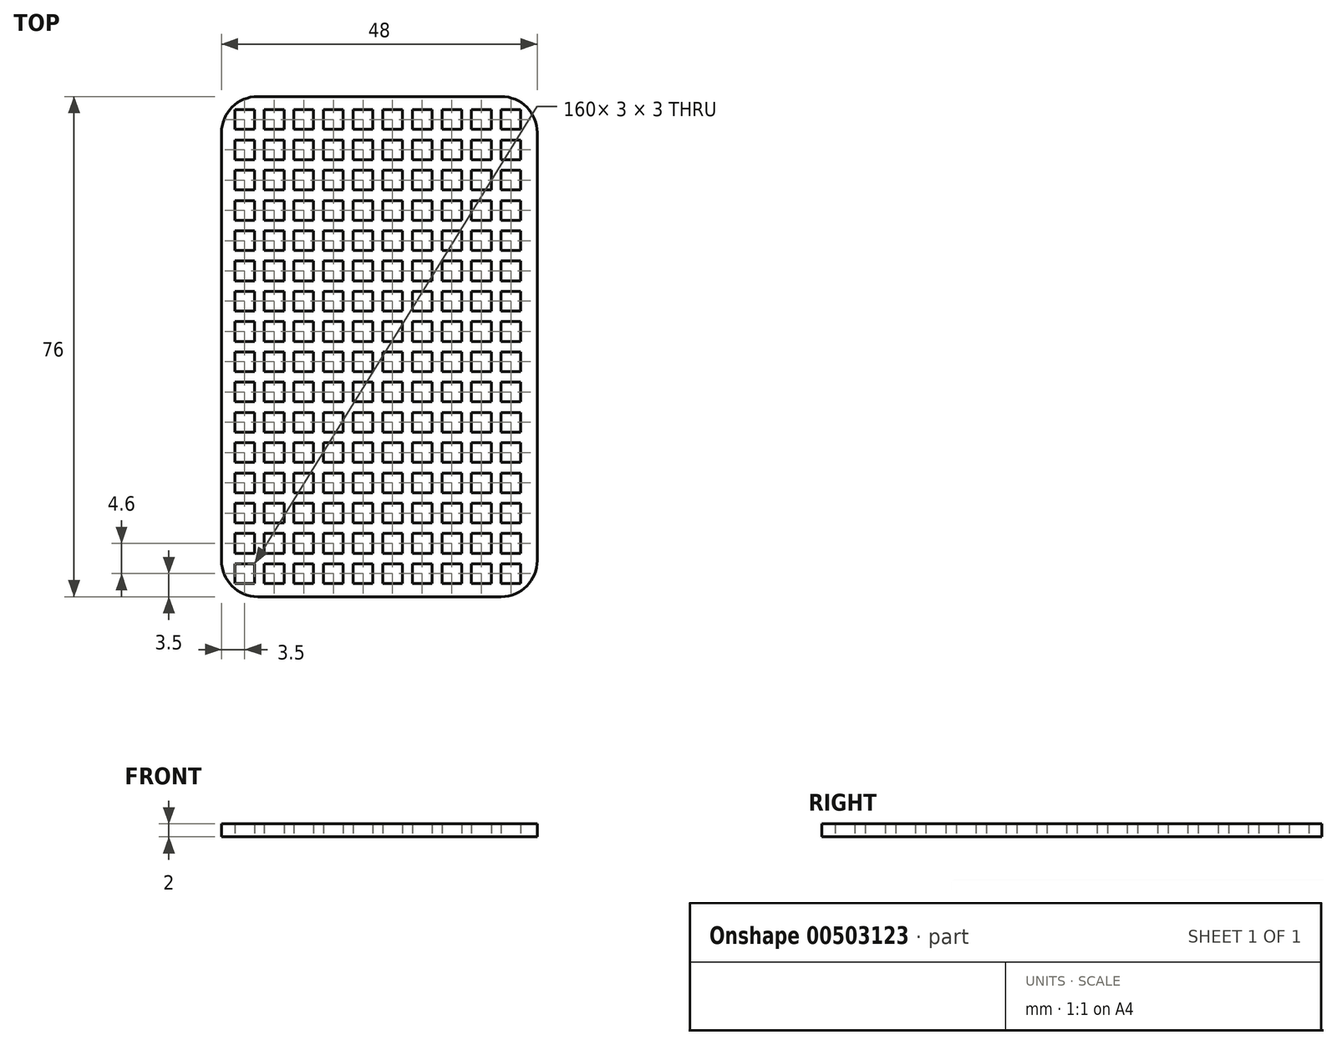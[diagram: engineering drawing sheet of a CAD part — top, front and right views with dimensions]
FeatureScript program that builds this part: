
annotation { "Feature Type Name" : "Feature", "Feature Type Description" : "" }
export const myFeature = defineFeature(function(context is Context, id is Id, definition is map)
    precondition{}
    {
        {
            var Q0;
            Q0=qCreatedBy(makeId("Top.planeOp"),FACE);
            var sketch = newSketch(context, id + "F0", { "sketchPlane" : qUnion([Q0])});
            skLineSegment(sketch, "E0.bottom", {"start": v(18.5, -38) * mm, "end": v(-18.5, -38) * mm});
            skLineSegment(sketch, "E0.top", {"start": v(18.5, 38) * mm, "end": v(-18.5, 38) * mm});
            skLineSegment(sketch, "E0.left", {"start": v(24, -32.5) * mm, "end": v(24, 32.5) * mm});
            skLineSegment(sketch, "E0.right", {"start": v(-24, -32.5) * mm, "end": v(-24, 32.5) * mm});
            skPoint(sketch, "E0.middle", {"position": v(-20.5, 34.5) * mm});
            skPoint(sketch, "E1.visualSharp", {"position": v(-24, 38) * mm});
            skArc(sketch, "E1.filletArc", {"start": v(-18.5, 38) * mm, "mid": v(-22.39, 36.39) * mm, "end": v(-24, 32.5) * mm});
            skPoint(sketch, "E2.visualSharp", {"position": v(24, 38) * mm});
            skArc(sketch, "E2.filletArc", {"start": v(24, 32.5) * mm, "mid": v(22.39, 36.39) * mm, "end": v(18.5, 38) * mm});
            skPoint(sketch, "E3.visualSharp", {"position": v(24, -38) * mm});
            skArc(sketch, "E3.filletArc", {"start": v(18.5, -38) * mm, "mid": v(22.39, -36.39) * mm, "end": v(24, -32.5) * mm});
            skPoint(sketch, "E4.visualSharp", {"position": v(-24, -38) * mm});
            skArc(sketch, "E4.filletArc", {"start": v(-24, -32.5) * mm, "mid": v(-22.39, -36.39) * mm, "end": v(-18.5, -38) * mm});
            skLineSegment(sketch, "E5.bottom", {"start": v(-19, 33) * mm, "end": v(-22, 33) * mm});
            skLineSegment(sketch, "E5.top", {"start": v(-19, 36) * mm, "end": v(-22, 36) * mm});
            skLineSegment(sketch, "E5.left", {"start": v(-19, 33) * mm, "end": v(-19, 36) * mm});
            skLineSegment(sketch, "E5.right", {"start": v(-22, 33) * mm, "end": v(-22, 36) * mm});
            skPoint(sketch, "E6", {"position": v(-22, 36) * mm});
            skPoint(sketch, "E7", {"position": v(52.1, 10.35) * mm});
            skPoint(sketch, "E8.0.1.0", {"position": v(-20.5, 29.9) * mm});
            skLineSegment(sketch, "E8.0.1.1", {"start": v(-22, 28.4) * mm, "end": v(-22, 31.4) * mm});
            skLineSegment(sketch, "E8.0.1.2", {"start": v(-19, 28.4) * mm, "end": v(-19, 31.4) * mm});
            skLineSegment(sketch, "E8.0.1.3", {"start": v(-19, 31.4) * mm, "end": v(-22, 31.4) * mm});
            skLineSegment(sketch, "E8.0.1.4", {"start": v(-19, 28.4) * mm, "end": v(-22, 28.4) * mm});
            skPoint(sketch, "E8.0.1.5", {"position": v(-22, 31.4) * mm});
            skPoint(sketch, "E8.0.1.6", {"position": v(-20.5, 29.9) * mm});
            skPoint(sketch, "E8.0.1.7", {"position": v(-20.5, 29.9) * mm});
            skPoint(sketch, "E8.0.2.0", {"position": v(-20.5, 25.3) * mm});
            skLineSegment(sketch, "E8.0.2.1", {"start": v(-22, 23.8) * mm, "end": v(-22, 26.8) * mm});
            skLineSegment(sketch, "E8.0.2.2", {"start": v(-19, 23.8) * mm, "end": v(-19, 26.8) * mm});
            skLineSegment(sketch, "E8.0.2.3", {"start": v(-19, 26.8) * mm, "end": v(-22, 26.8) * mm});
            skLineSegment(sketch, "E8.0.2.4", {"start": v(-19, 23.8) * mm, "end": v(-22, 23.8) * mm});
            skPoint(sketch, "E8.0.2.5", {"position": v(-22, 26.8) * mm});
            skPoint(sketch, "E8.0.2.6", {"position": v(-20.5, 25.3) * mm});
            skPoint(sketch, "E8.0.2.7", {"position": v(-20.5, 25.3) * mm});
            skPoint(sketch, "E8.0.3.0", {"position": v(-20.5, 20.7) * mm});
            skLineSegment(sketch, "E8.0.3.1", {"start": v(-22, 19.2) * mm, "end": v(-22, 22.2) * mm});
            skLineSegment(sketch, "E8.0.3.2", {"start": v(-19, 19.2) * mm, "end": v(-19, 22.2) * mm});
            skLineSegment(sketch, "E8.0.3.3", {"start": v(-19, 22.2) * mm, "end": v(-22, 22.2) * mm});
            skLineSegment(sketch, "E8.0.3.4", {"start": v(-19, 19.2) * mm, "end": v(-22, 19.2) * mm});
            skPoint(sketch, "E8.0.3.5", {"position": v(-22, 22.2) * mm});
            skPoint(sketch, "E8.0.3.6", {"position": v(-20.5, 20.7) * mm});
            skPoint(sketch, "E8.0.3.7", {"position": v(-20.5, 20.7) * mm});
            skPoint(sketch, "E8.0.4.0", {"position": v(-20.5, 16.1) * mm});
            skLineSegment(sketch, "E8.0.4.1", {"start": v(-22, 14.6) * mm, "end": v(-22, 17.6) * mm});
            skLineSegment(sketch, "E8.0.4.2", {"start": v(-19, 14.6) * mm, "end": v(-19, 17.6) * mm});
            skLineSegment(sketch, "E8.0.4.3", {"start": v(-19, 17.6) * mm, "end": v(-22, 17.6) * mm});
            skLineSegment(sketch, "E8.0.4.4", {"start": v(-19, 14.6) * mm, "end": v(-22, 14.6) * mm});
            skPoint(sketch, "E8.0.4.5", {"position": v(-22, 17.6) * mm});
            skPoint(sketch, "E8.0.4.6", {"position": v(-20.5, 16.1) * mm});
            skPoint(sketch, "E8.0.4.7", {"position": v(-20.5, 16.1) * mm});
            skPoint(sketch, "E8.0.5.0", {"position": v(-20.5, 11.5) * mm});
            skLineSegment(sketch, "E8.0.5.1", {"start": v(-22, 10) * mm, "end": v(-22, 13) * mm});
            skLineSegment(sketch, "E8.0.5.2", {"start": v(-19, 10) * mm, "end": v(-19, 13) * mm});
            skLineSegment(sketch, "E8.0.5.3", {"start": v(-19, 13) * mm, "end": v(-22, 13) * mm});
            skLineSegment(sketch, "E8.0.5.4", {"start": v(-19, 10) * mm, "end": v(-22, 10) * mm});
            skPoint(sketch, "E8.0.5.5", {"position": v(-22, 13) * mm});
            skPoint(sketch, "E8.0.5.6", {"position": v(-20.5, 11.5) * mm});
            skPoint(sketch, "E8.0.5.7", {"position": v(-20.5, 11.5) * mm});
            skPoint(sketch, "E8.0.6.0", {"position": v(-20.5, 6.9) * mm});
            skLineSegment(sketch, "E8.0.6.1", {"start": v(-22, 5.4) * mm, "end": v(-22, 8.4) * mm});
            skLineSegment(sketch, "E8.0.6.2", {"start": v(-19, 5.4) * mm, "end": v(-19, 8.4) * mm});
            skLineSegment(sketch, "E8.0.6.3", {"start": v(-19, 8.4) * mm, "end": v(-22, 8.4) * mm});
            skLineSegment(sketch, "E8.0.6.4", {"start": v(-19, 5.4) * mm, "end": v(-22, 5.4) * mm});
            skPoint(sketch, "E8.0.6.5", {"position": v(-22, 8.4) * mm});
            skPoint(sketch, "E8.0.6.6", {"position": v(-20.5, 6.9) * mm});
            skPoint(sketch, "E8.0.6.7", {"position": v(-20.5, 6.9) * mm});
            skPoint(sketch, "E8.0.7.0", {"position": v(-20.5, 2.3) * mm});
            skLineSegment(sketch, "E8.0.7.1", {"start": v(-22, 0.8) * mm, "end": v(-22, 3.8) * mm});
            skLineSegment(sketch, "E8.0.7.2", {"start": v(-19, 0.8) * mm, "end": v(-19, 3.8) * mm});
            skLineSegment(sketch, "E8.0.7.3", {"start": v(-19, 3.8) * mm, "end": v(-22, 3.8) * mm});
            skLineSegment(sketch, "E8.0.7.4", {"start": v(-19, 0.8) * mm, "end": v(-22, 0.8) * mm});
            skPoint(sketch, "E8.0.7.5", {"position": v(-22, 3.8) * mm});
            skPoint(sketch, "E8.0.7.6", {"position": v(-20.5, 2.3) * mm});
            skPoint(sketch, "E8.0.7.7", {"position": v(-20.5, 2.3) * mm});
            skPoint(sketch, "E8.0.8.0", {"position": v(-20.5, -2.3) * mm});
            skLineSegment(sketch, "E8.0.8.1", {"start": v(-22, -3.8) * mm, "end": v(-22, -0.8) * mm});
            skLineSegment(sketch, "E8.0.8.2", {"start": v(-19, -3.8) * mm, "end": v(-19, -0.8) * mm});
            skLineSegment(sketch, "E8.0.8.3", {"start": v(-19, -0.8) * mm, "end": v(-22, -0.8) * mm});
            skLineSegment(sketch, "E8.0.8.4", {"start": v(-19, -3.8) * mm, "end": v(-22, -3.8) * mm});
            skPoint(sketch, "E8.0.8.5", {"position": v(-22, -0.8) * mm});
            skPoint(sketch, "E8.0.8.6", {"position": v(-20.5, -2.3) * mm});
            skPoint(sketch, "E8.0.8.7", {"position": v(-20.5, -2.3) * mm});
            skPoint(sketch, "E8.0.9.0", {"position": v(-20.5, -6.9) * mm});
            skLineSegment(sketch, "E8.0.9.1", {"start": v(-22, -8.4) * mm, "end": v(-22, -5.4) * mm});
            skLineSegment(sketch, "E8.0.9.2", {"start": v(-19, -8.4) * mm, "end": v(-19, -5.4) * mm});
            skLineSegment(sketch, "E8.0.9.3", {"start": v(-19, -5.4) * mm, "end": v(-22, -5.4) * mm});
            skLineSegment(sketch, "E8.0.9.4", {"start": v(-19, -8.4) * mm, "end": v(-22, -8.4) * mm});
            skPoint(sketch, "E8.0.9.5", {"position": v(-22, -5.4) * mm});
            skPoint(sketch, "E8.0.9.6", {"position": v(-20.5, -6.9) * mm});
            skPoint(sketch, "E8.0.9.7", {"position": v(-20.5, -6.9) * mm});
            skPoint(sketch, "E8.0.10.0", {"position": v(-20.5, -11.5) * mm});
            skLineSegment(sketch, "E8.0.10.1", {"start": v(-22, -13) * mm, "end": v(-22, -10) * mm});
            skLineSegment(sketch, "E8.0.10.2", {"start": v(-19, -13) * mm, "end": v(-19, -10) * mm});
            skLineSegment(sketch, "E8.0.10.3", {"start": v(-19, -10) * mm, "end": v(-22, -10) * mm});
            skLineSegment(sketch, "E8.0.10.4", {"start": v(-19, -13) * mm, "end": v(-22, -13) * mm});
            skPoint(sketch, "E8.0.10.5", {"position": v(-22, -10) * mm});
            skPoint(sketch, "E8.0.10.6", {"position": v(-20.5, -11.5) * mm});
            skPoint(sketch, "E8.0.10.7", {"position": v(-20.5, -11.5) * mm});
            skPoint(sketch, "E8.0.11.0", {"position": v(-20.5, -16.1) * mm});
            skLineSegment(sketch, "E8.0.11.1", {"start": v(-22, -17.6) * mm, "end": v(-22, -14.6) * mm});
            skLineSegment(sketch, "E8.0.11.2", {"start": v(-19, -17.6) * mm, "end": v(-19, -14.6) * mm});
            skLineSegment(sketch, "E8.0.11.3", {"start": v(-19, -14.6) * mm, "end": v(-22, -14.6) * mm});
            skLineSegment(sketch, "E8.0.11.4", {"start": v(-19, -17.6) * mm, "end": v(-22, -17.6) * mm});
            skPoint(sketch, "E8.0.11.5", {"position": v(-22, -14.6) * mm});
            skPoint(sketch, "E8.0.11.6", {"position": v(-20.5, -16.1) * mm});
            skPoint(sketch, "E8.0.11.7", {"position": v(-20.5, -16.1) * mm});
            skPoint(sketch, "E8.0.12.0", {"position": v(-20.5, -20.7) * mm});
            skLineSegment(sketch, "E8.0.12.1", {"start": v(-22, -22.2) * mm, "end": v(-22, -19.2) * mm});
            skLineSegment(sketch, "E8.0.12.2", {"start": v(-19, -22.2) * mm, "end": v(-19, -19.2) * mm});
            skLineSegment(sketch, "E8.0.12.3", {"start": v(-19, -19.2) * mm, "end": v(-22, -19.2) * mm});
            skLineSegment(sketch, "E8.0.12.4", {"start": v(-19, -22.2) * mm, "end": v(-22, -22.2) * mm});
            skPoint(sketch, "E8.0.12.5", {"position": v(-22, -19.2) * mm});
            skPoint(sketch, "E8.0.12.6", {"position": v(-20.5, -20.7) * mm});
            skPoint(sketch, "E8.0.12.7", {"position": v(-20.5, -20.7) * mm});
            skPoint(sketch, "E8.0.13.0", {"position": v(-20.5, -25.3) * mm});
            skLineSegment(sketch, "E8.0.13.1", {"start": v(-22, -26.8) * mm, "end": v(-22, -23.8) * mm});
            skLineSegment(sketch, "E8.0.13.2", {"start": v(-19, -26.8) * mm, "end": v(-19, -23.8) * mm});
            skLineSegment(sketch, "E8.0.13.3", {"start": v(-19, -23.8) * mm, "end": v(-22, -23.8) * mm});
            skLineSegment(sketch, "E8.0.13.4", {"start": v(-19, -26.8) * mm, "end": v(-22, -26.8) * mm});
            skPoint(sketch, "E8.0.13.5", {"position": v(-22, -23.8) * mm});
            skPoint(sketch, "E8.0.13.6", {"position": v(-20.5, -25.3) * mm});
            skPoint(sketch, "E8.0.13.7", {"position": v(-20.5, -25.3) * mm});
            skPoint(sketch, "E8.0.14.0", {"position": v(-20.5, -29.9) * mm});
            skLineSegment(sketch, "E8.0.14.1", {"start": v(-22, -31.4) * mm, "end": v(-22, -28.4) * mm});
            skLineSegment(sketch, "E8.0.14.2", {"start": v(-19, -31.4) * mm, "end": v(-19, -28.4) * mm});
            skLineSegment(sketch, "E8.0.14.3", {"start": v(-19, -28.4) * mm, "end": v(-22, -28.4) * mm});
            skLineSegment(sketch, "E8.0.14.4", {"start": v(-19, -31.4) * mm, "end": v(-22, -31.4) * mm});
            skPoint(sketch, "E8.0.14.5", {"position": v(-22, -28.4) * mm});
            skPoint(sketch, "E8.0.14.6", {"position": v(-20.5, -29.9) * mm});
            skPoint(sketch, "E8.0.14.7", {"position": v(-20.5, -29.9) * mm});
            skPoint(sketch, "E8.0.15.0", {"position": v(-20.5, -34.5) * mm});
            skLineSegment(sketch, "E8.0.15.1", {"start": v(-22, -36) * mm, "end": v(-22, -33) * mm});
            skLineSegment(sketch, "E8.0.15.2", {"start": v(-19, -36) * mm, "end": v(-19, -33) * mm});
            skLineSegment(sketch, "E8.0.15.3", {"start": v(-19, -33) * mm, "end": v(-22, -33) * mm});
            skLineSegment(sketch, "E8.0.15.4", {"start": v(-19, -36) * mm, "end": v(-22, -36) * mm});
            skPoint(sketch, "E8.0.15.5", {"position": v(-22, -33) * mm});
            skPoint(sketch, "E8.0.15.6", {"position": v(-20.5, -34.5) * mm});
            skPoint(sketch, "E8.0.15.7", {"position": v(-20.5, -34.5) * mm});
            skPoint(sketch, "E8.1.0.0", {"position": v(-16, 34.5) * mm});
            skLineSegment(sketch, "E8.1.0.1", {"start": v(-17.5, 33) * mm, "end": v(-17.5, 36) * mm});
            skLineSegment(sketch, "E8.1.0.2", {"start": v(-14.5, 33) * mm, "end": v(-14.5, 36) * mm});
            skLineSegment(sketch, "E8.1.0.3", {"start": v(-14.5, 36) * mm, "end": v(-17.5, 36) * mm});
            skLineSegment(sketch, "E8.1.0.4", {"start": v(-14.5, 33) * mm, "end": v(-17.5, 33) * mm});
            skPoint(sketch, "E8.1.0.5", {"position": v(-17.5, 36) * mm});
            skPoint(sketch, "E8.1.0.6", {"position": v(-16, 34.5) * mm});
            skPoint(sketch, "E8.1.0.7", {"position": v(-16, 34.5) * mm});
            skPoint(sketch, "E8.1.1.0", {"position": v(-16, 29.9) * mm});
            skLineSegment(sketch, "E8.1.1.1", {"start": v(-17.5, 28.4) * mm, "end": v(-17.5, 31.4) * mm});
            skLineSegment(sketch, "E8.1.1.2", {"start": v(-14.5, 28.4) * mm, "end": v(-14.5, 31.4) * mm});
            skLineSegment(sketch, "E8.1.1.3", {"start": v(-14.5, 31.4) * mm, "end": v(-17.5, 31.4) * mm});
            skLineSegment(sketch, "E8.1.1.4", {"start": v(-14.5, 28.4) * mm, "end": v(-17.5, 28.4) * mm});
            skPoint(sketch, "E8.1.1.5", {"position": v(-17.5, 31.4) * mm});
            skPoint(sketch, "E8.1.1.6", {"position": v(-16, 29.9) * mm});
            skPoint(sketch, "E8.1.1.7", {"position": v(-16, 29.9) * mm});
            skPoint(sketch, "E8.1.2.0", {"position": v(-16, 25.3) * mm});
            skLineSegment(sketch, "E8.1.2.1", {"start": v(-17.5, 23.8) * mm, "end": v(-17.5, 26.8) * mm});
            skLineSegment(sketch, "E8.1.2.2", {"start": v(-14.5, 23.8) * mm, "end": v(-14.5, 26.8) * mm});
            skLineSegment(sketch, "E8.1.2.3", {"start": v(-14.5, 26.8) * mm, "end": v(-17.5, 26.8) * mm});
            skLineSegment(sketch, "E8.1.2.4", {"start": v(-14.5, 23.8) * mm, "end": v(-17.5, 23.8) * mm});
            skPoint(sketch, "E8.1.2.5", {"position": v(-17.5, 26.8) * mm});
            skPoint(sketch, "E8.1.2.6", {"position": v(-16, 25.3) * mm});
            skPoint(sketch, "E8.1.2.7", {"position": v(-16, 25.3) * mm});
            skPoint(sketch, "E8.1.3.0", {"position": v(-16, 20.7) * mm});
            skLineSegment(sketch, "E8.1.3.1", {"start": v(-17.5, 19.2) * mm, "end": v(-17.5, 22.2) * mm});
            skLineSegment(sketch, "E8.1.3.2", {"start": v(-14.5, 19.2) * mm, "end": v(-14.5, 22.2) * mm});
            skLineSegment(sketch, "E8.1.3.3", {"start": v(-14.5, 22.2) * mm, "end": v(-17.5, 22.2) * mm});
            skLineSegment(sketch, "E8.1.3.4", {"start": v(-14.5, 19.2) * mm, "end": v(-17.5, 19.2) * mm});
            skPoint(sketch, "E8.1.3.5", {"position": v(-17.5, 22.2) * mm});
            skPoint(sketch, "E8.1.3.6", {"position": v(-16, 20.7) * mm});
            skPoint(sketch, "E8.1.3.7", {"position": v(-16, 20.7) * mm});
            skPoint(sketch, "E8.1.4.0", {"position": v(-16, 16.1) * mm});
            skLineSegment(sketch, "E8.1.4.1", {"start": v(-17.5, 14.6) * mm, "end": v(-17.5, 17.6) * mm});
            skLineSegment(sketch, "E8.1.4.2", {"start": v(-14.5, 14.6) * mm, "end": v(-14.5, 17.6) * mm});
            skLineSegment(sketch, "E8.1.4.3", {"start": v(-14.5, 17.6) * mm, "end": v(-17.5, 17.6) * mm});
            skLineSegment(sketch, "E8.1.4.4", {"start": v(-14.5, 14.6) * mm, "end": v(-17.5, 14.6) * mm});
            skPoint(sketch, "E8.1.4.5", {"position": v(-17.5, 17.6) * mm});
            skPoint(sketch, "E8.1.4.6", {"position": v(-16, 16.1) * mm});
            skPoint(sketch, "E8.1.4.7", {"position": v(-16, 16.1) * mm});
            skPoint(sketch, "E8.1.5.0", {"position": v(-16, 11.5) * mm});
            skLineSegment(sketch, "E8.1.5.1", {"start": v(-17.5, 10) * mm, "end": v(-17.5, 13) * mm});
            skLineSegment(sketch, "E8.1.5.2", {"start": v(-14.5, 10) * mm, "end": v(-14.5, 13) * mm});
            skLineSegment(sketch, "E8.1.5.3", {"start": v(-14.5, 13) * mm, "end": v(-17.5, 13) * mm});
            skLineSegment(sketch, "E8.1.5.4", {"start": v(-14.5, 10) * mm, "end": v(-17.5, 10) * mm});
            skPoint(sketch, "E8.1.5.5", {"position": v(-17.5, 13) * mm});
            skPoint(sketch, "E8.1.5.6", {"position": v(-16, 11.5) * mm});
            skPoint(sketch, "E8.1.5.7", {"position": v(-16, 11.5) * mm});
            skPoint(sketch, "E8.1.6.0", {"position": v(-16, 6.9) * mm});
            skLineSegment(sketch, "E8.1.6.1", {"start": v(-17.5, 5.4) * mm, "end": v(-17.5, 8.4) * mm});
            skLineSegment(sketch, "E8.1.6.2", {"start": v(-14.5, 5.4) * mm, "end": v(-14.5, 8.4) * mm});
            skLineSegment(sketch, "E8.1.6.3", {"start": v(-14.5, 8.4) * mm, "end": v(-17.5, 8.4) * mm});
            skLineSegment(sketch, "E8.1.6.4", {"start": v(-14.5, 5.4) * mm, "end": v(-17.5, 5.4) * mm});
            skPoint(sketch, "E8.1.6.5", {"position": v(-17.5, 8.4) * mm});
            skPoint(sketch, "E8.1.6.6", {"position": v(-16, 6.9) * mm});
            skPoint(sketch, "E8.1.6.7", {"position": v(-16, 6.9) * mm});
            skPoint(sketch, "E8.1.7.0", {"position": v(-16, 2.3) * mm});
            skLineSegment(sketch, "E8.1.7.1", {"start": v(-17.5, 0.8) * mm, "end": v(-17.5, 3.8) * mm});
            skLineSegment(sketch, "E8.1.7.2", {"start": v(-14.5, 0.8) * mm, "end": v(-14.5, 3.8) * mm});
            skLineSegment(sketch, "E8.1.7.3", {"start": v(-14.5, 3.8) * mm, "end": v(-17.5, 3.8) * mm});
            skLineSegment(sketch, "E8.1.7.4", {"start": v(-14.5, 0.8) * mm, "end": v(-17.5, 0.8) * mm});
            skPoint(sketch, "E8.1.7.5", {"position": v(-17.5, 3.8) * mm});
            skPoint(sketch, "E8.1.7.6", {"position": v(-16, 2.3) * mm});
            skPoint(sketch, "E8.1.7.7", {"position": v(-16, 2.3) * mm});
            skPoint(sketch, "E8.1.8.0", {"position": v(-16, -2.3) * mm});
            skLineSegment(sketch, "E8.1.8.1", {"start": v(-17.5, -3.8) * mm, "end": v(-17.5, -0.8) * mm});
            skLineSegment(sketch, "E8.1.8.2", {"start": v(-14.5, -3.8) * mm, "end": v(-14.5, -0.8) * mm});
            skLineSegment(sketch, "E8.1.8.3", {"start": v(-14.5, -0.8) * mm, "end": v(-17.5, -0.8) * mm});
            skLineSegment(sketch, "E8.1.8.4", {"start": v(-14.5, -3.8) * mm, "end": v(-17.5, -3.8) * mm});
            skPoint(sketch, "E8.1.8.5", {"position": v(-17.5, -0.8) * mm});
            skPoint(sketch, "E8.1.8.6", {"position": v(-16, -2.3) * mm});
            skPoint(sketch, "E8.1.8.7", {"position": v(-16, -2.3) * mm});
            skPoint(sketch, "E8.1.9.0", {"position": v(-16, -6.9) * mm});
            skLineSegment(sketch, "E8.1.9.1", {"start": v(-17.5, -8.4) * mm, "end": v(-17.5, -5.4) * mm});
            skLineSegment(sketch, "E8.1.9.2", {"start": v(-14.5, -8.4) * mm, "end": v(-14.5, -5.4) * mm});
            skLineSegment(sketch, "E8.1.9.3", {"start": v(-14.5, -5.4) * mm, "end": v(-17.5, -5.4) * mm});
            skLineSegment(sketch, "E8.1.9.4", {"start": v(-14.5, -8.4) * mm, "end": v(-17.5, -8.4) * mm});
            skPoint(sketch, "E8.1.9.5", {"position": v(-17.5, -5.4) * mm});
            skPoint(sketch, "E8.1.9.6", {"position": v(-16, -6.9) * mm});
            skPoint(sketch, "E8.1.9.7", {"position": v(-16, -6.9) * mm});
            skPoint(sketch, "E8.1.10.0", {"position": v(-16, -11.5) * mm});
            skLineSegment(sketch, "E8.1.10.1", {"start": v(-17.5, -13) * mm, "end": v(-17.5, -10) * mm});
            skLineSegment(sketch, "E8.1.10.2", {"start": v(-14.5, -13) * mm, "end": v(-14.5, -10) * mm});
            skLineSegment(sketch, "E8.1.10.3", {"start": v(-14.5, -10) * mm, "end": v(-17.5, -10) * mm});
            skLineSegment(sketch, "E8.1.10.4", {"start": v(-14.5, -13) * mm, "end": v(-17.5, -13) * mm});
            skPoint(sketch, "E8.1.10.5", {"position": v(-17.5, -10) * mm});
            skPoint(sketch, "E8.1.10.6", {"position": v(-16, -11.5) * mm});
            skPoint(sketch, "E8.1.10.7", {"position": v(-16, -11.5) * mm});
            skPoint(sketch, "E8.1.11.0", {"position": v(-16, -16.1) * mm});
            skLineSegment(sketch, "E8.1.11.1", {"start": v(-17.5, -17.6) * mm, "end": v(-17.5, -14.6) * mm});
            skLineSegment(sketch, "E8.1.11.2", {"start": v(-14.5, -17.6) * mm, "end": v(-14.5, -14.6) * mm});
            skLineSegment(sketch, "E8.1.11.3", {"start": v(-14.5, -14.6) * mm, "end": v(-17.5, -14.6) * mm});
            skLineSegment(sketch, "E8.1.11.4", {"start": v(-14.5, -17.6) * mm, "end": v(-17.5, -17.6) * mm});
            skPoint(sketch, "E8.1.11.5", {"position": v(-17.5, -14.6) * mm});
            skPoint(sketch, "E8.1.11.6", {"position": v(-16, -16.1) * mm});
            skPoint(sketch, "E8.1.11.7", {"position": v(-16, -16.1) * mm});
            skPoint(sketch, "E8.1.12.0", {"position": v(-16, -20.7) * mm});
            skLineSegment(sketch, "E8.1.12.1", {"start": v(-17.5, -22.2) * mm, "end": v(-17.5, -19.2) * mm});
            skLineSegment(sketch, "E8.1.12.2", {"start": v(-14.5, -22.2) * mm, "end": v(-14.5, -19.2) * mm});
            skLineSegment(sketch, "E8.1.12.3", {"start": v(-14.5, -19.2) * mm, "end": v(-17.5, -19.2) * mm});
            skLineSegment(sketch, "E8.1.12.4", {"start": v(-14.5, -22.2) * mm, "end": v(-17.5, -22.2) * mm});
            skPoint(sketch, "E8.1.12.5", {"position": v(-17.5, -19.2) * mm});
            skPoint(sketch, "E8.1.12.6", {"position": v(-16, -20.7) * mm});
            skPoint(sketch, "E8.1.12.7", {"position": v(-16, -20.7) * mm});
            skPoint(sketch, "E8.1.13.0", {"position": v(-16, -25.3) * mm});
            skLineSegment(sketch, "E8.1.13.1", {"start": v(-17.5, -26.8) * mm, "end": v(-17.5, -23.8) * mm});
            skLineSegment(sketch, "E8.1.13.2", {"start": v(-14.5, -26.8) * mm, "end": v(-14.5, -23.8) * mm});
            skLineSegment(sketch, "E8.1.13.3", {"start": v(-14.5, -23.8) * mm, "end": v(-17.5, -23.8) * mm});
            skLineSegment(sketch, "E8.1.13.4", {"start": v(-14.5, -26.8) * mm, "end": v(-17.5, -26.8) * mm});
            skPoint(sketch, "E8.1.13.5", {"position": v(-17.5, -23.8) * mm});
            skPoint(sketch, "E8.1.13.6", {"position": v(-16, -25.3) * mm});
            skPoint(sketch, "E8.1.13.7", {"position": v(-16, -25.3) * mm});
            skPoint(sketch, "E8.1.14.0", {"position": v(-16, -29.9) * mm});
            skLineSegment(sketch, "E8.1.14.1", {"start": v(-17.5, -31.4) * mm, "end": v(-17.5, -28.4) * mm});
            skLineSegment(sketch, "E8.1.14.2", {"start": v(-14.5, -31.4) * mm, "end": v(-14.5, -28.4) * mm});
            skLineSegment(sketch, "E8.1.14.3", {"start": v(-14.5, -28.4) * mm, "end": v(-17.5, -28.4) * mm});
            skLineSegment(sketch, "E8.1.14.4", {"start": v(-14.5, -31.4) * mm, "end": v(-17.5, -31.4) * mm});
            skPoint(sketch, "E8.1.14.5", {"position": v(-17.5, -28.4) * mm});
            skPoint(sketch, "E8.1.14.6", {"position": v(-16, -29.9) * mm});
            skPoint(sketch, "E8.1.14.7", {"position": v(-16, -29.9) * mm});
            skPoint(sketch, "E8.1.15.0", {"position": v(-16, -34.5) * mm});
            skLineSegment(sketch, "E8.1.15.1", {"start": v(-17.5, -36) * mm, "end": v(-17.5, -33) * mm});
            skLineSegment(sketch, "E8.1.15.2", {"start": v(-14.5, -36) * mm, "end": v(-14.5, -33) * mm});
            skLineSegment(sketch, "E8.1.15.3", {"start": v(-14.5, -33) * mm, "end": v(-17.5, -33) * mm});
            skLineSegment(sketch, "E8.1.15.4", {"start": v(-14.5, -36) * mm, "end": v(-17.5, -36) * mm});
            skPoint(sketch, "E8.1.15.5", {"position": v(-17.5, -33) * mm});
            skPoint(sketch, "E8.1.15.6", {"position": v(-16, -34.5) * mm});
            skPoint(sketch, "E8.1.15.7", {"position": v(-16, -34.5) * mm});
            skPoint(sketch, "E8.2.0.0", {"position": v(-11.5, 34.5) * mm});
            skLineSegment(sketch, "E8.2.0.1", {"start": v(-13, 33) * mm, "end": v(-13, 36) * mm});
            skLineSegment(sketch, "E8.2.0.2", {"start": v(-10, 33) * mm, "end": v(-10, 36) * mm});
            skLineSegment(sketch, "E8.2.0.3", {"start": v(-10, 36) * mm, "end": v(-13, 36) * mm});
            skLineSegment(sketch, "E8.2.0.4", {"start": v(-10, 33) * mm, "end": v(-13, 33) * mm});
            skPoint(sketch, "E8.2.0.5", {"position": v(-13, 36) * mm});
            skPoint(sketch, "E8.2.0.6", {"position": v(-11.5, 34.5) * mm});
            skPoint(sketch, "E8.2.0.7", {"position": v(-11.5, 34.5) * mm});
            skPoint(sketch, "E8.2.1.0", {"position": v(-11.5, 29.9) * mm});
            skLineSegment(sketch, "E8.2.1.1", {"start": v(-13, 28.4) * mm, "end": v(-13, 31.4) * mm});
            skLineSegment(sketch, "E8.2.1.2", {"start": v(-10, 28.4) * mm, "end": v(-10, 31.4) * mm});
            skLineSegment(sketch, "E8.2.1.3", {"start": v(-10, 31.4) * mm, "end": v(-13, 31.4) * mm});
            skLineSegment(sketch, "E8.2.1.4", {"start": v(-10, 28.4) * mm, "end": v(-13, 28.4) * mm});
            skPoint(sketch, "E8.2.1.5", {"position": v(-13, 31.4) * mm});
            skPoint(sketch, "E8.2.1.6", {"position": v(-11.5, 29.9) * mm});
            skPoint(sketch, "E8.2.1.7", {"position": v(-11.5, 29.9) * mm});
            skPoint(sketch, "E8.2.2.0", {"position": v(-11.5, 25.3) * mm});
            skLineSegment(sketch, "E8.2.2.1", {"start": v(-13, 23.8) * mm, "end": v(-13, 26.8) * mm});
            skLineSegment(sketch, "E8.2.2.2", {"start": v(-10, 23.8) * mm, "end": v(-10, 26.8) * mm});
            skLineSegment(sketch, "E8.2.2.3", {"start": v(-10, 26.8) * mm, "end": v(-13, 26.8) * mm});
            skLineSegment(sketch, "E8.2.2.4", {"start": v(-10, 23.8) * mm, "end": v(-13, 23.8) * mm});
            skPoint(sketch, "E8.2.2.5", {"position": v(-13, 26.8) * mm});
            skPoint(sketch, "E8.2.2.6", {"position": v(-11.5, 25.3) * mm});
            skPoint(sketch, "E8.2.2.7", {"position": v(-11.5, 25.3) * mm});
            skPoint(sketch, "E8.2.3.0", {"position": v(-11.5, 20.7) * mm});
            skLineSegment(sketch, "E8.2.3.1", {"start": v(-13, 19.2) * mm, "end": v(-13, 22.2) * mm});
            skLineSegment(sketch, "E8.2.3.2", {"start": v(-10, 19.2) * mm, "end": v(-10, 22.2) * mm});
            skLineSegment(sketch, "E8.2.3.3", {"start": v(-10, 22.2) * mm, "end": v(-13, 22.2) * mm});
            skLineSegment(sketch, "E8.2.3.4", {"start": v(-10, 19.2) * mm, "end": v(-13, 19.2) * mm});
            skPoint(sketch, "E8.2.3.5", {"position": v(-13, 22.2) * mm});
            skPoint(sketch, "E8.2.3.6", {"position": v(-11.5, 20.7) * mm});
            skPoint(sketch, "E8.2.3.7", {"position": v(-11.5, 20.7) * mm});
            skPoint(sketch, "E8.2.4.0", {"position": v(-11.5, 16.1) * mm});
            skLineSegment(sketch, "E8.2.4.1", {"start": v(-13, 14.6) * mm, "end": v(-13, 17.6) * mm});
            skLineSegment(sketch, "E8.2.4.2", {"start": v(-10, 14.6) * mm, "end": v(-10, 17.6) * mm});
            skLineSegment(sketch, "E8.2.4.3", {"start": v(-10, 17.6) * mm, "end": v(-13, 17.6) * mm});
            skLineSegment(sketch, "E8.2.4.4", {"start": v(-10, 14.6) * mm, "end": v(-13, 14.6) * mm});
            skPoint(sketch, "E8.2.4.5", {"position": v(-13, 17.6) * mm});
            skPoint(sketch, "E8.2.4.6", {"position": v(-11.5, 16.1) * mm});
            skPoint(sketch, "E8.2.4.7", {"position": v(-11.5, 16.1) * mm});
            skPoint(sketch, "E8.2.5.0", {"position": v(-11.5, 11.5) * mm});
            skLineSegment(sketch, "E8.2.5.1", {"start": v(-13, 10) * mm, "end": v(-13, 13) * mm});
            skLineSegment(sketch, "E8.2.5.2", {"start": v(-10, 10) * mm, "end": v(-10, 13) * mm});
            skLineSegment(sketch, "E8.2.5.3", {"start": v(-10, 13) * mm, "end": v(-13, 13) * mm});
            skLineSegment(sketch, "E8.2.5.4", {"start": v(-10, 10) * mm, "end": v(-13, 10) * mm});
            skPoint(sketch, "E8.2.5.5", {"position": v(-13, 13) * mm});
            skPoint(sketch, "E8.2.5.6", {"position": v(-11.5, 11.5) * mm});
            skPoint(sketch, "E8.2.5.7", {"position": v(-11.5, 11.5) * mm});
            skPoint(sketch, "E8.2.6.0", {"position": v(-11.5, 6.9) * mm});
            skLineSegment(sketch, "E8.2.6.1", {"start": v(-13, 5.4) * mm, "end": v(-13, 8.4) * mm});
            skLineSegment(sketch, "E8.2.6.2", {"start": v(-10, 5.4) * mm, "end": v(-10, 8.4) * mm});
            skLineSegment(sketch, "E8.2.6.3", {"start": v(-10, 8.4) * mm, "end": v(-13, 8.4) * mm});
            skLineSegment(sketch, "E8.2.6.4", {"start": v(-10, 5.4) * mm, "end": v(-13, 5.4) * mm});
            skPoint(sketch, "E8.2.6.5", {"position": v(-13, 8.4) * mm});
            skPoint(sketch, "E8.2.6.6", {"position": v(-11.5, 6.9) * mm});
            skPoint(sketch, "E8.2.6.7", {"position": v(-11.5, 6.9) * mm});
            skPoint(sketch, "E8.2.7.0", {"position": v(-11.5, 2.3) * mm});
            skLineSegment(sketch, "E8.2.7.1", {"start": v(-13, 0.8) * mm, "end": v(-13, 3.8) * mm});
            skLineSegment(sketch, "E8.2.7.2", {"start": v(-10, 0.8) * mm, "end": v(-10, 3.8) * mm});
            skLineSegment(sketch, "E8.2.7.3", {"start": v(-10, 3.8) * mm, "end": v(-13, 3.8) * mm});
            skLineSegment(sketch, "E8.2.7.4", {"start": v(-10, 0.8) * mm, "end": v(-13, 0.8) * mm});
            skPoint(sketch, "E8.2.7.5", {"position": v(-13, 3.8) * mm});
            skPoint(sketch, "E8.2.7.6", {"position": v(-11.5, 2.3) * mm});
            skPoint(sketch, "E8.2.7.7", {"position": v(-11.5, 2.3) * mm});
            skPoint(sketch, "E8.2.8.0", {"position": v(-11.5, -2.3) * mm});
            skLineSegment(sketch, "E8.2.8.1", {"start": v(-13, -3.8) * mm, "end": v(-13, -0.8) * mm});
            skLineSegment(sketch, "E8.2.8.2", {"start": v(-10, -3.8) * mm, "end": v(-10, -0.8) * mm});
            skLineSegment(sketch, "E8.2.8.3", {"start": v(-10, -0.8) * mm, "end": v(-13, -0.8) * mm});
            skLineSegment(sketch, "E8.2.8.4", {"start": v(-10, -3.8) * mm, "end": v(-13, -3.8) * mm});
            skPoint(sketch, "E8.2.8.5", {"position": v(-13, -0.8) * mm});
            skPoint(sketch, "E8.2.8.6", {"position": v(-11.5, -2.3) * mm});
            skPoint(sketch, "E8.2.8.7", {"position": v(-11.5, -2.3) * mm});
            skPoint(sketch, "E8.2.9.0", {"position": v(-11.5, -6.9) * mm});
            skLineSegment(sketch, "E8.2.9.1", {"start": v(-13, -8.4) * mm, "end": v(-13, -5.4) * mm});
            skLineSegment(sketch, "E8.2.9.2", {"start": v(-10, -8.4) * mm, "end": v(-10, -5.4) * mm});
            skLineSegment(sketch, "E8.2.9.3", {"start": v(-10, -5.4) * mm, "end": v(-13, -5.4) * mm});
            skLineSegment(sketch, "E8.2.9.4", {"start": v(-10, -8.4) * mm, "end": v(-13, -8.4) * mm});
            skPoint(sketch, "E8.2.9.5", {"position": v(-13, -5.4) * mm});
            skPoint(sketch, "E8.2.9.6", {"position": v(-11.5, -6.9) * mm});
            skPoint(sketch, "E8.2.9.7", {"position": v(-11.5, -6.9) * mm});
            skPoint(sketch, "E8.2.10.0", {"position": v(-11.5, -11.5) * mm});
            skLineSegment(sketch, "E8.2.10.1", {"start": v(-13, -13) * mm, "end": v(-13, -10) * mm});
            skLineSegment(sketch, "E8.2.10.2", {"start": v(-10, -13) * mm, "end": v(-10, -10) * mm});
            skLineSegment(sketch, "E8.2.10.3", {"start": v(-10, -10) * mm, "end": v(-13, -10) * mm});
            skLineSegment(sketch, "E8.2.10.4", {"start": v(-10, -13) * mm, "end": v(-13, -13) * mm});
            skPoint(sketch, "E8.2.10.5", {"position": v(-13, -10) * mm});
            skPoint(sketch, "E8.2.10.6", {"position": v(-11.5, -11.5) * mm});
            skPoint(sketch, "E8.2.10.7", {"position": v(-11.5, -11.5) * mm});
            skPoint(sketch, "E8.2.11.0", {"position": v(-11.5, -16.1) * mm});
            skLineSegment(sketch, "E8.2.11.1", {"start": v(-13, -17.6) * mm, "end": v(-13, -14.6) * mm});
            skLineSegment(sketch, "E8.2.11.2", {"start": v(-10, -17.6) * mm, "end": v(-10, -14.6) * mm});
            skLineSegment(sketch, "E8.2.11.3", {"start": v(-10, -14.6) * mm, "end": v(-13, -14.6) * mm});
            skLineSegment(sketch, "E8.2.11.4", {"start": v(-10, -17.6) * mm, "end": v(-13, -17.6) * mm});
            skPoint(sketch, "E8.2.11.5", {"position": v(-13, -14.6) * mm});
            skPoint(sketch, "E8.2.11.6", {"position": v(-11.5, -16.1) * mm});
            skPoint(sketch, "E8.2.11.7", {"position": v(-11.5, -16.1) * mm});
            skPoint(sketch, "E8.2.12.0", {"position": v(-11.5, -20.7) * mm});
            skLineSegment(sketch, "E8.2.12.1", {"start": v(-13, -22.2) * mm, "end": v(-13, -19.2) * mm});
            skLineSegment(sketch, "E8.2.12.2", {"start": v(-10, -22.2) * mm, "end": v(-10, -19.2) * mm});
            skLineSegment(sketch, "E8.2.12.3", {"start": v(-10, -19.2) * mm, "end": v(-13, -19.2) * mm});
            skLineSegment(sketch, "E8.2.12.4", {"start": v(-10, -22.2) * mm, "end": v(-13, -22.2) * mm});
            skPoint(sketch, "E8.2.12.5", {"position": v(-13, -19.2) * mm});
            skPoint(sketch, "E8.2.12.6", {"position": v(-11.5, -20.7) * mm});
            skPoint(sketch, "E8.2.12.7", {"position": v(-11.5, -20.7) * mm});
            skPoint(sketch, "E8.2.13.0", {"position": v(-11.5, -25.3) * mm});
            skLineSegment(sketch, "E8.2.13.1", {"start": v(-13, -26.8) * mm, "end": v(-13, -23.8) * mm});
            skLineSegment(sketch, "E8.2.13.2", {"start": v(-10, -26.8) * mm, "end": v(-10, -23.8) * mm});
            skLineSegment(sketch, "E8.2.13.3", {"start": v(-10, -23.8) * mm, "end": v(-13, -23.8) * mm});
            skLineSegment(sketch, "E8.2.13.4", {"start": v(-10, -26.8) * mm, "end": v(-13, -26.8) * mm});
            skPoint(sketch, "E8.2.13.5", {"position": v(-13, -23.8) * mm});
            skPoint(sketch, "E8.2.13.6", {"position": v(-11.5, -25.3) * mm});
            skPoint(sketch, "E8.2.13.7", {"position": v(-11.5, -25.3) * mm});
            skPoint(sketch, "E8.2.14.0", {"position": v(-11.5, -29.9) * mm});
            skLineSegment(sketch, "E8.2.14.1", {"start": v(-13, -31.4) * mm, "end": v(-13, -28.4) * mm});
            skLineSegment(sketch, "E8.2.14.2", {"start": v(-10, -31.4) * mm, "end": v(-10, -28.4) * mm});
            skLineSegment(sketch, "E8.2.14.3", {"start": v(-10, -28.4) * mm, "end": v(-13, -28.4) * mm});
            skLineSegment(sketch, "E8.2.14.4", {"start": v(-10, -31.4) * mm, "end": v(-13, -31.4) * mm});
            skPoint(sketch, "E8.2.14.5", {"position": v(-13, -28.4) * mm});
            skPoint(sketch, "E8.2.14.6", {"position": v(-11.5, -29.9) * mm});
            skPoint(sketch, "E8.2.14.7", {"position": v(-11.5, -29.9) * mm});
            skPoint(sketch, "E8.2.15.0", {"position": v(-11.5, -34.5) * mm});
            skLineSegment(sketch, "E8.2.15.1", {"start": v(-13, -36) * mm, "end": v(-13, -33) * mm});
            skLineSegment(sketch, "E8.2.15.2", {"start": v(-10, -36) * mm, "end": v(-10, -33) * mm});
            skLineSegment(sketch, "E8.2.15.3", {"start": v(-10, -33) * mm, "end": v(-13, -33) * mm});
            skLineSegment(sketch, "E8.2.15.4", {"start": v(-10, -36) * mm, "end": v(-13, -36) * mm});
            skPoint(sketch, "E8.2.15.5", {"position": v(-13, -33) * mm});
            skPoint(sketch, "E8.2.15.6", {"position": v(-11.5, -34.5) * mm});
            skPoint(sketch, "E8.2.15.7", {"position": v(-11.5, -34.5) * mm});
            skPoint(sketch, "E8.3.0.0", {"position": v(-7, 34.5) * mm});
            skLineSegment(sketch, "E8.3.0.1", {"start": v(-8.5, 33) * mm, "end": v(-8.5, 36) * mm});
            skLineSegment(sketch, "E8.3.0.2", {"start": v(-5.5, 33) * mm, "end": v(-5.5, 36) * mm});
            skLineSegment(sketch, "E8.3.0.3", {"start": v(-5.5, 36) * mm, "end": v(-8.5, 36) * mm});
            skLineSegment(sketch, "E8.3.0.4", {"start": v(-5.5, 33) * mm, "end": v(-8.5, 33) * mm});
            skPoint(sketch, "E8.3.0.5", {"position": v(-8.5, 36) * mm});
            skPoint(sketch, "E8.3.0.6", {"position": v(-7, 34.5) * mm});
            skPoint(sketch, "E8.3.0.7", {"position": v(-7, 34.5) * mm});
            skPoint(sketch, "E8.3.1.0", {"position": v(-7, 29.9) * mm});
            skLineSegment(sketch, "E8.3.1.1", {"start": v(-8.5, 28.4) * mm, "end": v(-8.5, 31.4) * mm});
            skLineSegment(sketch, "E8.3.1.2", {"start": v(-5.5, 28.4) * mm, "end": v(-5.5, 31.4) * mm});
            skLineSegment(sketch, "E8.3.1.3", {"start": v(-5.5, 31.4) * mm, "end": v(-8.5, 31.4) * mm});
            skLineSegment(sketch, "E8.3.1.4", {"start": v(-5.5, 28.4) * mm, "end": v(-8.5, 28.4) * mm});
            skPoint(sketch, "E8.3.1.5", {"position": v(-8.5, 31.4) * mm});
            skPoint(sketch, "E8.3.1.6", {"position": v(-7, 29.9) * mm});
            skPoint(sketch, "E8.3.1.7", {"position": v(-7, 29.9) * mm});
            skPoint(sketch, "E8.3.2.0", {"position": v(-7, 25.3) * mm});
            skLineSegment(sketch, "E8.3.2.1", {"start": v(-8.5, 23.8) * mm, "end": v(-8.5, 26.8) * mm});
            skLineSegment(sketch, "E8.3.2.2", {"start": v(-5.5, 23.8) * mm, "end": v(-5.5, 26.8) * mm});
            skLineSegment(sketch, "E8.3.2.3", {"start": v(-5.5, 26.8) * mm, "end": v(-8.5, 26.8) * mm});
            skLineSegment(sketch, "E8.3.2.4", {"start": v(-5.5, 23.8) * mm, "end": v(-8.5, 23.8) * mm});
            skPoint(sketch, "E8.3.2.5", {"position": v(-8.5, 26.8) * mm});
            skPoint(sketch, "E8.3.2.6", {"position": v(-7, 25.3) * mm});
            skPoint(sketch, "E8.3.2.7", {"position": v(-7, 25.3) * mm});
            skPoint(sketch, "E8.3.3.0", {"position": v(-7, 20.7) * mm});
            skLineSegment(sketch, "E8.3.3.1", {"start": v(-8.5, 19.2) * mm, "end": v(-8.5, 22.2) * mm});
            skLineSegment(sketch, "E8.3.3.2", {"start": v(-5.5, 19.2) * mm, "end": v(-5.5, 22.2) * mm});
            skLineSegment(sketch, "E8.3.3.3", {"start": v(-5.5, 22.2) * mm, "end": v(-8.5, 22.2) * mm});
            skLineSegment(sketch, "E8.3.3.4", {"start": v(-5.5, 19.2) * mm, "end": v(-8.5, 19.2) * mm});
            skPoint(sketch, "E8.3.3.5", {"position": v(-8.5, 22.2) * mm});
            skPoint(sketch, "E8.3.3.6", {"position": v(-7, 20.7) * mm});
            skPoint(sketch, "E8.3.3.7", {"position": v(-7, 20.7) * mm});
            skPoint(sketch, "E8.3.4.0", {"position": v(-7, 16.1) * mm});
            skLineSegment(sketch, "E8.3.4.1", {"start": v(-8.5, 14.6) * mm, "end": v(-8.5, 17.6) * mm});
            skLineSegment(sketch, "E8.3.4.2", {"start": v(-5.5, 14.6) * mm, "end": v(-5.5, 17.6) * mm});
            skLineSegment(sketch, "E8.3.4.3", {"start": v(-5.5, 17.6) * mm, "end": v(-8.5, 17.6) * mm});
            skLineSegment(sketch, "E8.3.4.4", {"start": v(-5.5, 14.6) * mm, "end": v(-8.5, 14.6) * mm});
            skPoint(sketch, "E8.3.4.5", {"position": v(-8.5, 17.6) * mm});
            skPoint(sketch, "E8.3.4.6", {"position": v(-7, 16.1) * mm});
            skPoint(sketch, "E8.3.4.7", {"position": v(-7, 16.1) * mm});
            skPoint(sketch, "E8.3.5.0", {"position": v(-7, 11.5) * mm});
            skLineSegment(sketch, "E8.3.5.1", {"start": v(-8.5, 10) * mm, "end": v(-8.5, 13) * mm});
            skLineSegment(sketch, "E8.3.5.2", {"start": v(-5.5, 10) * mm, "end": v(-5.5, 13) * mm});
            skLineSegment(sketch, "E8.3.5.3", {"start": v(-5.5, 13) * mm, "end": v(-8.5, 13) * mm});
            skLineSegment(sketch, "E8.3.5.4", {"start": v(-5.5, 10) * mm, "end": v(-8.5, 10) * mm});
            skPoint(sketch, "E8.3.5.5", {"position": v(-8.5, 13) * mm});
            skPoint(sketch, "E8.3.5.6", {"position": v(-7, 11.5) * mm});
            skPoint(sketch, "E8.3.5.7", {"position": v(-7, 11.5) * mm});
            skPoint(sketch, "E8.3.6.0", {"position": v(-7, 6.9) * mm});
            skLineSegment(sketch, "E8.3.6.1", {"start": v(-8.5, 5.4) * mm, "end": v(-8.5, 8.4) * mm});
            skLineSegment(sketch, "E8.3.6.2", {"start": v(-5.5, 5.4) * mm, "end": v(-5.5, 8.4) * mm});
            skLineSegment(sketch, "E8.3.6.3", {"start": v(-5.5, 8.4) * mm, "end": v(-8.5, 8.4) * mm});
            skLineSegment(sketch, "E8.3.6.4", {"start": v(-5.5, 5.4) * mm, "end": v(-8.5, 5.4) * mm});
            skPoint(sketch, "E8.3.6.5", {"position": v(-8.5, 8.4) * mm});
            skPoint(sketch, "E8.3.6.6", {"position": v(-7, 6.9) * mm});
            skPoint(sketch, "E8.3.6.7", {"position": v(-7, 6.9) * mm});
            skPoint(sketch, "E8.3.7.0", {"position": v(-7, 2.3) * mm});
            skLineSegment(sketch, "E8.3.7.1", {"start": v(-8.5, 0.8) * mm, "end": v(-8.5, 3.8) * mm});
            skLineSegment(sketch, "E8.3.7.2", {"start": v(-5.5, 0.8) * mm, "end": v(-5.5, 3.8) * mm});
            skLineSegment(sketch, "E8.3.7.3", {"start": v(-5.5, 3.8) * mm, "end": v(-8.5, 3.8) * mm});
            skLineSegment(sketch, "E8.3.7.4", {"start": v(-5.5, 0.8) * mm, "end": v(-8.5, 0.8) * mm});
            skPoint(sketch, "E8.3.7.5", {"position": v(-8.5, 3.8) * mm});
            skPoint(sketch, "E8.3.7.6", {"position": v(-7, 2.3) * mm});
            skPoint(sketch, "E8.3.7.7", {"position": v(-7, 2.3) * mm});
            skPoint(sketch, "E8.3.8.0", {"position": v(-7, -2.3) * mm});
            skLineSegment(sketch, "E8.3.8.1", {"start": v(-8.5, -3.8) * mm, "end": v(-8.5, -0.8) * mm});
            skLineSegment(sketch, "E8.3.8.2", {"start": v(-5.5, -3.8) * mm, "end": v(-5.5, -0.8) * mm});
            skLineSegment(sketch, "E8.3.8.3", {"start": v(-5.5, -0.8) * mm, "end": v(-8.5, -0.8) * mm});
            skLineSegment(sketch, "E8.3.8.4", {"start": v(-5.5, -3.8) * mm, "end": v(-8.5, -3.8) * mm});
            skPoint(sketch, "E8.3.8.5", {"position": v(-8.5, -0.8) * mm});
            skPoint(sketch, "E8.3.8.6", {"position": v(-7, -2.3) * mm});
            skPoint(sketch, "E8.3.8.7", {"position": v(-7, -2.3) * mm});
            skPoint(sketch, "E8.3.9.0", {"position": v(-7, -6.9) * mm});
            skLineSegment(sketch, "E8.3.9.1", {"start": v(-8.5, -8.4) * mm, "end": v(-8.5, -5.4) * mm});
            skLineSegment(sketch, "E8.3.9.2", {"start": v(-5.5, -8.4) * mm, "end": v(-5.5, -5.4) * mm});
            skLineSegment(sketch, "E8.3.9.3", {"start": v(-5.5, -5.4) * mm, "end": v(-8.5, -5.4) * mm});
            skLineSegment(sketch, "E8.3.9.4", {"start": v(-5.5, -8.4) * mm, "end": v(-8.5, -8.4) * mm});
            skPoint(sketch, "E8.3.9.5", {"position": v(-8.5, -5.4) * mm});
            skPoint(sketch, "E8.3.9.6", {"position": v(-7, -6.9) * mm});
            skPoint(sketch, "E8.3.9.7", {"position": v(-7, -6.9) * mm});
            skPoint(sketch, "E8.3.10.0", {"position": v(-7, -11.5) * mm});
            skLineSegment(sketch, "E8.3.10.1", {"start": v(-8.5, -13) * mm, "end": v(-8.5, -10) * mm});
            skLineSegment(sketch, "E8.3.10.2", {"start": v(-5.5, -13) * mm, "end": v(-5.5, -10) * mm});
            skLineSegment(sketch, "E8.3.10.3", {"start": v(-5.5, -10) * mm, "end": v(-8.5, -10) * mm});
            skLineSegment(sketch, "E8.3.10.4", {"start": v(-5.5, -13) * mm, "end": v(-8.5, -13) * mm});
            skPoint(sketch, "E8.3.10.5", {"position": v(-8.5, -10) * mm});
            skPoint(sketch, "E8.3.10.6", {"position": v(-7, -11.5) * mm});
            skPoint(sketch, "E8.3.10.7", {"position": v(-7, -11.5) * mm});
            skPoint(sketch, "E8.3.11.0", {"position": v(-7, -16.1) * mm});
            skLineSegment(sketch, "E8.3.11.1", {"start": v(-8.5, -17.6) * mm, "end": v(-8.5, -14.6) * mm});
            skLineSegment(sketch, "E8.3.11.2", {"start": v(-5.5, -17.6) * mm, "end": v(-5.5, -14.6) * mm});
            skLineSegment(sketch, "E8.3.11.3", {"start": v(-5.5, -14.6) * mm, "end": v(-8.5, -14.6) * mm});
            skLineSegment(sketch, "E8.3.11.4", {"start": v(-5.5, -17.6) * mm, "end": v(-8.5, -17.6) * mm});
            skPoint(sketch, "E8.3.11.5", {"position": v(-8.5, -14.6) * mm});
            skPoint(sketch, "E8.3.11.6", {"position": v(-7, -16.1) * mm});
            skPoint(sketch, "E8.3.11.7", {"position": v(-7, -16.1) * mm});
            skPoint(sketch, "E8.3.12.0", {"position": v(-7, -20.7) * mm});
            skLineSegment(sketch, "E8.3.12.1", {"start": v(-8.5, -22.2) * mm, "end": v(-8.5, -19.2) * mm});
            skLineSegment(sketch, "E8.3.12.2", {"start": v(-5.5, -22.2) * mm, "end": v(-5.5, -19.2) * mm});
            skLineSegment(sketch, "E8.3.12.3", {"start": v(-5.5, -19.2) * mm, "end": v(-8.5, -19.2) * mm});
            skLineSegment(sketch, "E8.3.12.4", {"start": v(-5.5, -22.2) * mm, "end": v(-8.5, -22.2) * mm});
            skPoint(sketch, "E8.3.12.5", {"position": v(-8.5, -19.2) * mm});
            skPoint(sketch, "E8.3.12.6", {"position": v(-7, -20.7) * mm});
            skPoint(sketch, "E8.3.12.7", {"position": v(-7, -20.7) * mm});
            skPoint(sketch, "E8.3.13.0", {"position": v(-7, -25.3) * mm});
            skLineSegment(sketch, "E8.3.13.1", {"start": v(-8.5, -26.8) * mm, "end": v(-8.5, -23.8) * mm});
            skLineSegment(sketch, "E8.3.13.2", {"start": v(-5.5, -26.8) * mm, "end": v(-5.5, -23.8) * mm});
            skLineSegment(sketch, "E8.3.13.3", {"start": v(-5.5, -23.8) * mm, "end": v(-8.5, -23.8) * mm});
            skLineSegment(sketch, "E8.3.13.4", {"start": v(-5.5, -26.8) * mm, "end": v(-8.5, -26.8) * mm});
            skPoint(sketch, "E8.3.13.5", {"position": v(-8.5, -23.8) * mm});
            skPoint(sketch, "E8.3.13.6", {"position": v(-7, -25.3) * mm});
            skPoint(sketch, "E8.3.13.7", {"position": v(-7, -25.3) * mm});
            skPoint(sketch, "E8.3.14.0", {"position": v(-7, -29.9) * mm});
            skLineSegment(sketch, "E8.3.14.1", {"start": v(-8.5, -31.4) * mm, "end": v(-8.5, -28.4) * mm});
            skLineSegment(sketch, "E8.3.14.2", {"start": v(-5.5, -31.4) * mm, "end": v(-5.5, -28.4) * mm});
            skLineSegment(sketch, "E8.3.14.3", {"start": v(-5.5, -28.4) * mm, "end": v(-8.5, -28.4) * mm});
            skLineSegment(sketch, "E8.3.14.4", {"start": v(-5.5, -31.4) * mm, "end": v(-8.5, -31.4) * mm});
            skPoint(sketch, "E8.3.14.5", {"position": v(-8.5, -28.4) * mm});
            skPoint(sketch, "E8.3.14.6", {"position": v(-7, -29.9) * mm});
            skPoint(sketch, "E8.3.14.7", {"position": v(-7, -29.9) * mm});
            skPoint(sketch, "E8.3.15.0", {"position": v(-7, -34.5) * mm});
            skLineSegment(sketch, "E8.3.15.1", {"start": v(-8.5, -36) * mm, "end": v(-8.5, -33) * mm});
            skLineSegment(sketch, "E8.3.15.2", {"start": v(-5.5, -36) * mm, "end": v(-5.5, -33) * mm});
            skLineSegment(sketch, "E8.3.15.3", {"start": v(-5.5, -33) * mm, "end": v(-8.5, -33) * mm});
            skLineSegment(sketch, "E8.3.15.4", {"start": v(-5.5, -36) * mm, "end": v(-8.5, -36) * mm});
            skPoint(sketch, "E8.3.15.5", {"position": v(-8.5, -33) * mm});
            skPoint(sketch, "E8.3.15.6", {"position": v(-7, -34.5) * mm});
            skPoint(sketch, "E8.3.15.7", {"position": v(-7, -34.5) * mm});
            skPoint(sketch, "E8.4.0.0", {"position": v(-2.5, 34.5) * mm});
            skLineSegment(sketch, "E8.4.0.1", {"start": v(-4, 33) * mm, "end": v(-4, 36) * mm});
            skLineSegment(sketch, "E8.4.0.2", {"start": v(-1, 33) * mm, "end": v(-1, 36) * mm});
            skLineSegment(sketch, "E8.4.0.3", {"start": v(-1, 36) * mm, "end": v(-4, 36) * mm});
            skLineSegment(sketch, "E8.4.0.4", {"start": v(-1, 33) * mm, "end": v(-4, 33) * mm});
            skPoint(sketch, "E8.4.0.5", {"position": v(-4, 36) * mm});
            skPoint(sketch, "E8.4.0.6", {"position": v(-2.5, 34.5) * mm});
            skPoint(sketch, "E8.4.0.7", {"position": v(-2.5, 34.5) * mm});
            skPoint(sketch, "E8.4.1.0", {"position": v(-2.5, 29.9) * mm});
            skLineSegment(sketch, "E8.4.1.1", {"start": v(-4, 28.4) * mm, "end": v(-4, 31.4) * mm});
            skLineSegment(sketch, "E8.4.1.2", {"start": v(-1, 28.4) * mm, "end": v(-1, 31.4) * mm});
            skLineSegment(sketch, "E8.4.1.3", {"start": v(-1, 31.4) * mm, "end": v(-4, 31.4) * mm});
            skLineSegment(sketch, "E8.4.1.4", {"start": v(-1, 28.4) * mm, "end": v(-4, 28.4) * mm});
            skPoint(sketch, "E8.4.1.5", {"position": v(-4, 31.4) * mm});
            skPoint(sketch, "E8.4.1.6", {"position": v(-2.5, 29.9) * mm});
            skPoint(sketch, "E8.4.1.7", {"position": v(-2.5, 29.9) * mm});
            skPoint(sketch, "E8.4.2.0", {"position": v(-2.5, 25.3) * mm});
            skLineSegment(sketch, "E8.4.2.1", {"start": v(-4, 23.8) * mm, "end": v(-4, 26.8) * mm});
            skLineSegment(sketch, "E8.4.2.2", {"start": v(-1, 23.8) * mm, "end": v(-1, 26.8) * mm});
            skLineSegment(sketch, "E8.4.2.3", {"start": v(-1, 26.8) * mm, "end": v(-4, 26.8) * mm});
            skLineSegment(sketch, "E8.4.2.4", {"start": v(-1, 23.8) * mm, "end": v(-4, 23.8) * mm});
            skPoint(sketch, "E8.4.2.5", {"position": v(-4, 26.8) * mm});
            skPoint(sketch, "E8.4.2.6", {"position": v(-2.5, 25.3) * mm});
            skPoint(sketch, "E8.4.2.7", {"position": v(-2.5, 25.3) * mm});
            skPoint(sketch, "E8.4.3.0", {"position": v(-2.5, 20.7) * mm});
            skLineSegment(sketch, "E8.4.3.1", {"start": v(-4, 19.2) * mm, "end": v(-4, 22.2) * mm});
            skLineSegment(sketch, "E8.4.3.2", {"start": v(-1, 19.2) * mm, "end": v(-1, 22.2) * mm});
            skLineSegment(sketch, "E8.4.3.3", {"start": v(-1, 22.2) * mm, "end": v(-4, 22.2) * mm});
            skLineSegment(sketch, "E8.4.3.4", {"start": v(-1, 19.2) * mm, "end": v(-4, 19.2) * mm});
            skPoint(sketch, "E8.4.3.5", {"position": v(-4, 22.2) * mm});
            skPoint(sketch, "E8.4.3.6", {"position": v(-2.5, 20.7) * mm});
            skPoint(sketch, "E8.4.3.7", {"position": v(-2.5, 20.7) * mm});
            skPoint(sketch, "E8.4.4.0", {"position": v(-2.5, 16.1) * mm});
            skLineSegment(sketch, "E8.4.4.1", {"start": v(-4, 14.6) * mm, "end": v(-4, 17.6) * mm});
            skLineSegment(sketch, "E8.4.4.2", {"start": v(-1, 14.6) * mm, "end": v(-1, 17.6) * mm});
            skLineSegment(sketch, "E8.4.4.3", {"start": v(-1, 17.6) * mm, "end": v(-4, 17.6) * mm});
            skLineSegment(sketch, "E8.4.4.4", {"start": v(-1, 14.6) * mm, "end": v(-4, 14.6) * mm});
            skPoint(sketch, "E8.4.4.5", {"position": v(-4, 17.6) * mm});
            skPoint(sketch, "E8.4.4.6", {"position": v(-2.5, 16.1) * mm});
            skPoint(sketch, "E8.4.4.7", {"position": v(-2.5, 16.1) * mm});
            skPoint(sketch, "E8.4.5.0", {"position": v(-2.5, 11.5) * mm});
            skLineSegment(sketch, "E8.4.5.1", {"start": v(-4, 10) * mm, "end": v(-4, 13) * mm});
            skLineSegment(sketch, "E8.4.5.2", {"start": v(-1, 10) * mm, "end": v(-1, 13) * mm});
            skLineSegment(sketch, "E8.4.5.3", {"start": v(-1, 13) * mm, "end": v(-4, 13) * mm});
            skLineSegment(sketch, "E8.4.5.4", {"start": v(-1, 10) * mm, "end": v(-4, 10) * mm});
            skPoint(sketch, "E8.4.5.5", {"position": v(-4, 13) * mm});
            skPoint(sketch, "E8.4.5.6", {"position": v(-2.5, 11.5) * mm});
            skPoint(sketch, "E8.4.5.7", {"position": v(-2.5, 11.5) * mm});
            skPoint(sketch, "E8.4.6.0", {"position": v(-2.5, 6.9) * mm});
            skLineSegment(sketch, "E8.4.6.1", {"start": v(-4, 5.4) * mm, "end": v(-4, 8.4) * mm});
            skLineSegment(sketch, "E8.4.6.2", {"start": v(-1, 5.4) * mm, "end": v(-1, 8.4) * mm});
            skLineSegment(sketch, "E8.4.6.3", {"start": v(-1, 8.4) * mm, "end": v(-4, 8.4) * mm});
            skLineSegment(sketch, "E8.4.6.4", {"start": v(-1, 5.4) * mm, "end": v(-4, 5.4) * mm});
            skPoint(sketch, "E8.4.6.5", {"position": v(-4, 8.4) * mm});
            skPoint(sketch, "E8.4.6.6", {"position": v(-2.5, 6.9) * mm});
            skPoint(sketch, "E8.4.6.7", {"position": v(-2.5, 6.9) * mm});
            skPoint(sketch, "E8.4.7.0", {"position": v(-2.5, 2.3) * mm});
            skLineSegment(sketch, "E8.4.7.1", {"start": v(-4, 0.8) * mm, "end": v(-4, 3.8) * mm});
            skLineSegment(sketch, "E8.4.7.2", {"start": v(-1, 0.8) * mm, "end": v(-1, 3.8) * mm});
            skLineSegment(sketch, "E8.4.7.3", {"start": v(-1, 3.8) * mm, "end": v(-4, 3.8) * mm});
            skLineSegment(sketch, "E8.4.7.4", {"start": v(-1, 0.8) * mm, "end": v(-4, 0.8) * mm});
            skPoint(sketch, "E8.4.7.5", {"position": v(-4, 3.8) * mm});
            skPoint(sketch, "E8.4.7.6", {"position": v(-2.5, 2.3) * mm});
            skPoint(sketch, "E8.4.7.7", {"position": v(-2.5, 2.3) * mm});
            skPoint(sketch, "E8.4.8.0", {"position": v(-2.5, -2.3) * mm});
            skLineSegment(sketch, "E8.4.8.1", {"start": v(-4, -3.8) * mm, "end": v(-4, -0.8) * mm});
            skLineSegment(sketch, "E8.4.8.2", {"start": v(-1, -3.8) * mm, "end": v(-1, -0.8) * mm});
            skLineSegment(sketch, "E8.4.8.3", {"start": v(-1, -0.8) * mm, "end": v(-4, -0.8) * mm});
            skLineSegment(sketch, "E8.4.8.4", {"start": v(-1, -3.8) * mm, "end": v(-4, -3.8) * mm});
            skPoint(sketch, "E8.4.8.5", {"position": v(-4, -0.8) * mm});
            skPoint(sketch, "E8.4.8.6", {"position": v(-2.5, -2.3) * mm});
            skPoint(sketch, "E8.4.8.7", {"position": v(-2.5, -2.3) * mm});
            skPoint(sketch, "E8.4.9.0", {"position": v(-2.5, -6.9) * mm});
            skLineSegment(sketch, "E8.4.9.1", {"start": v(-4, -8.4) * mm, "end": v(-4, -5.4) * mm});
            skLineSegment(sketch, "E8.4.9.2", {"start": v(-1, -8.4) * mm, "end": v(-1, -5.4) * mm});
            skLineSegment(sketch, "E8.4.9.3", {"start": v(-1, -5.4) * mm, "end": v(-4, -5.4) * mm});
            skLineSegment(sketch, "E8.4.9.4", {"start": v(-1, -8.4) * mm, "end": v(-4, -8.4) * mm});
            skPoint(sketch, "E8.4.9.5", {"position": v(-4, -5.4) * mm});
            skPoint(sketch, "E8.4.9.6", {"position": v(-2.5, -6.9) * mm});
            skPoint(sketch, "E8.4.9.7", {"position": v(-2.5, -6.9) * mm});
            skPoint(sketch, "E8.4.10.0", {"position": v(-2.5, -11.5) * mm});
            skLineSegment(sketch, "E8.4.10.1", {"start": v(-4, -13) * mm, "end": v(-4, -10) * mm});
            skLineSegment(sketch, "E8.4.10.2", {"start": v(-1, -13) * mm, "end": v(-1, -10) * mm});
            skLineSegment(sketch, "E8.4.10.3", {"start": v(-1, -10) * mm, "end": v(-4, -10) * mm});
            skLineSegment(sketch, "E8.4.10.4", {"start": v(-1, -13) * mm, "end": v(-4, -13) * mm});
            skPoint(sketch, "E8.4.10.5", {"position": v(-4, -10) * mm});
            skPoint(sketch, "E8.4.10.6", {"position": v(-2.5, -11.5) * mm});
            skPoint(sketch, "E8.4.10.7", {"position": v(-2.5, -11.5) * mm});
            skPoint(sketch, "E8.4.11.0", {"position": v(-2.5, -16.1) * mm});
            skLineSegment(sketch, "E8.4.11.1", {"start": v(-4, -17.6) * mm, "end": v(-4, -14.6) * mm});
            skLineSegment(sketch, "E8.4.11.2", {"start": v(-1, -17.6) * mm, "end": v(-1, -14.6) * mm});
            skLineSegment(sketch, "E8.4.11.3", {"start": v(-1, -14.6) * mm, "end": v(-4, -14.6) * mm});
            skLineSegment(sketch, "E8.4.11.4", {"start": v(-1, -17.6) * mm, "end": v(-4, -17.6) * mm});
            skPoint(sketch, "E8.4.11.5", {"position": v(-4, -14.6) * mm});
            skPoint(sketch, "E8.4.11.6", {"position": v(-2.5, -16.1) * mm});
            skPoint(sketch, "E8.4.11.7", {"position": v(-2.5, -16.1) * mm});
            skPoint(sketch, "E8.4.12.0", {"position": v(-2.5, -20.7) * mm});
            skLineSegment(sketch, "E8.4.12.1", {"start": v(-4, -22.2) * mm, "end": v(-4, -19.2) * mm});
            skLineSegment(sketch, "E8.4.12.2", {"start": v(-1, -22.2) * mm, "end": v(-1, -19.2) * mm});
            skLineSegment(sketch, "E8.4.12.3", {"start": v(-1, -19.2) * mm, "end": v(-4, -19.2) * mm});
            skLineSegment(sketch, "E8.4.12.4", {"start": v(-1, -22.2) * mm, "end": v(-4, -22.2) * mm});
            skPoint(sketch, "E8.4.12.5", {"position": v(-4, -19.2) * mm});
            skPoint(sketch, "E8.4.12.6", {"position": v(-2.5, -20.7) * mm});
            skPoint(sketch, "E8.4.12.7", {"position": v(-2.5, -20.7) * mm});
            skPoint(sketch, "E8.4.13.0", {"position": v(-2.5, -25.3) * mm});
            skLineSegment(sketch, "E8.4.13.1", {"start": v(-4, -26.8) * mm, "end": v(-4, -23.8) * mm});
            skLineSegment(sketch, "E8.4.13.2", {"start": v(-1, -26.8) * mm, "end": v(-1, -23.8) * mm});
            skLineSegment(sketch, "E8.4.13.3", {"start": v(-1, -23.8) * mm, "end": v(-4, -23.8) * mm});
            skLineSegment(sketch, "E8.4.13.4", {"start": v(-1, -26.8) * mm, "end": v(-4, -26.8) * mm});
            skPoint(sketch, "E8.4.13.5", {"position": v(-4, -23.8) * mm});
            skPoint(sketch, "E8.4.13.6", {"position": v(-2.5, -25.3) * mm});
            skPoint(sketch, "E8.4.13.7", {"position": v(-2.5, -25.3) * mm});
            skPoint(sketch, "E8.4.14.0", {"position": v(-2.5, -29.9) * mm});
            skLineSegment(sketch, "E8.4.14.1", {"start": v(-4, -31.4) * mm, "end": v(-4, -28.4) * mm});
            skLineSegment(sketch, "E8.4.14.2", {"start": v(-1, -31.4) * mm, "end": v(-1, -28.4) * mm});
            skLineSegment(sketch, "E8.4.14.3", {"start": v(-1, -28.4) * mm, "end": v(-4, -28.4) * mm});
            skLineSegment(sketch, "E8.4.14.4", {"start": v(-1, -31.4) * mm, "end": v(-4, -31.4) * mm});
            skPoint(sketch, "E8.4.14.5", {"position": v(-4, -28.4) * mm});
            skPoint(sketch, "E8.4.14.6", {"position": v(-2.5, -29.9) * mm});
            skPoint(sketch, "E8.4.14.7", {"position": v(-2.5, -29.9) * mm});
            skPoint(sketch, "E8.4.15.0", {"position": v(-2.5, -34.5) * mm});
            skLineSegment(sketch, "E8.4.15.1", {"start": v(-4, -36) * mm, "end": v(-4, -33) * mm});
            skLineSegment(sketch, "E8.4.15.2", {"start": v(-1, -36) * mm, "end": v(-1, -33) * mm});
            skLineSegment(sketch, "E8.4.15.3", {"start": v(-1, -33) * mm, "end": v(-4, -33) * mm});
            skLineSegment(sketch, "E8.4.15.4", {"start": v(-1, -36) * mm, "end": v(-4, -36) * mm});
            skPoint(sketch, "E8.4.15.5", {"position": v(-4, -33) * mm});
            skPoint(sketch, "E8.4.15.6", {"position": v(-2.5, -34.5) * mm});
            skPoint(sketch, "E8.4.15.7", {"position": v(-2.5, -34.5) * mm});
            skPoint(sketch, "E8.5.0.0", {"position": v(2, 34.5) * mm});
            skLineSegment(sketch, "E8.5.0.1", {"start": v(0.5, 33) * mm, "end": v(0.5, 36) * mm});
            skLineSegment(sketch, "E8.5.0.2", {"start": v(3.5, 33) * mm, "end": v(3.5, 36) * mm});
            skLineSegment(sketch, "E8.5.0.3", {"start": v(3.5, 36) * mm, "end": v(0.5, 36) * mm});
            skLineSegment(sketch, "E8.5.0.4", {"start": v(3.5, 33) * mm, "end": v(0.5, 33) * mm});
            skPoint(sketch, "E8.5.0.5", {"position": v(0.5, 36) * mm});
            skPoint(sketch, "E8.5.0.6", {"position": v(2, 34.5) * mm});
            skPoint(sketch, "E8.5.0.7", {"position": v(2, 34.5) * mm});
            skPoint(sketch, "E8.5.1.0", {"position": v(2, 29.9) * mm});
            skLineSegment(sketch, "E8.5.1.1", {"start": v(0.5, 28.4) * mm, "end": v(0.5, 31.4) * mm});
            skLineSegment(sketch, "E8.5.1.2", {"start": v(3.5, 28.4) * mm, "end": v(3.5, 31.4) * mm});
            skLineSegment(sketch, "E8.5.1.3", {"start": v(3.5, 31.4) * mm, "end": v(0.5, 31.4) * mm});
            skLineSegment(sketch, "E8.5.1.4", {"start": v(3.5, 28.4) * mm, "end": v(0.5, 28.4) * mm});
            skPoint(sketch, "E8.5.1.5", {"position": v(0.5, 31.4) * mm});
            skPoint(sketch, "E8.5.1.6", {"position": v(2, 29.9) * mm});
            skPoint(sketch, "E8.5.1.7", {"position": v(2, 29.9) * mm});
            skPoint(sketch, "E8.5.2.0", {"position": v(2, 25.3) * mm});
            skLineSegment(sketch, "E8.5.2.1", {"start": v(0.5, 23.8) * mm, "end": v(0.5, 26.8) * mm});
            skLineSegment(sketch, "E8.5.2.2", {"start": v(3.5, 23.8) * mm, "end": v(3.5, 26.8) * mm});
            skLineSegment(sketch, "E8.5.2.3", {"start": v(3.5, 26.8) * mm, "end": v(0.5, 26.8) * mm});
            skLineSegment(sketch, "E8.5.2.4", {"start": v(3.5, 23.8) * mm, "end": v(0.5, 23.8) * mm});
            skPoint(sketch, "E8.5.2.5", {"position": v(0.5, 26.8) * mm});
            skPoint(sketch, "E8.5.2.6", {"position": v(2, 25.3) * mm});
            skPoint(sketch, "E8.5.2.7", {"position": v(2, 25.3) * mm});
            skPoint(sketch, "E8.5.3.0", {"position": v(2, 20.7) * mm});
            skLineSegment(sketch, "E8.5.3.1", {"start": v(0.5, 19.2) * mm, "end": v(0.5, 22.2) * mm});
            skLineSegment(sketch, "E8.5.3.2", {"start": v(3.5, 19.2) * mm, "end": v(3.5, 22.2) * mm});
            skLineSegment(sketch, "E8.5.3.3", {"start": v(3.5, 22.2) * mm, "end": v(0.5, 22.2) * mm});
            skLineSegment(sketch, "E8.5.3.4", {"start": v(3.5, 19.2) * mm, "end": v(0.5, 19.2) * mm});
            skPoint(sketch, "E8.5.3.5", {"position": v(0.5, 22.2) * mm});
            skPoint(sketch, "E8.5.3.6", {"position": v(2, 20.7) * mm});
            skPoint(sketch, "E8.5.3.7", {"position": v(2, 20.7) * mm});
            skPoint(sketch, "E8.5.4.0", {"position": v(2, 16.1) * mm});
            skLineSegment(sketch, "E8.5.4.1", {"start": v(0.5, 14.6) * mm, "end": v(0.5, 17.6) * mm});
            skLineSegment(sketch, "E8.5.4.2", {"start": v(3.5, 14.6) * mm, "end": v(3.5, 17.6) * mm});
            skLineSegment(sketch, "E8.5.4.3", {"start": v(3.5, 17.6) * mm, "end": v(0.5, 17.6) * mm});
            skLineSegment(sketch, "E8.5.4.4", {"start": v(3.5, 14.6) * mm, "end": v(0.5, 14.6) * mm});
            skPoint(sketch, "E8.5.4.5", {"position": v(0.5, 17.6) * mm});
            skPoint(sketch, "E8.5.4.6", {"position": v(2, 16.1) * mm});
            skPoint(sketch, "E8.5.4.7", {"position": v(2, 16.1) * mm});
            skPoint(sketch, "E8.5.5.0", {"position": v(2, 11.5) * mm});
            skLineSegment(sketch, "E8.5.5.1", {"start": v(0.5, 10) * mm, "end": v(0.5, 13) * mm});
            skLineSegment(sketch, "E8.5.5.2", {"start": v(3.5, 10) * mm, "end": v(3.5, 13) * mm});
            skLineSegment(sketch, "E8.5.5.3", {"start": v(3.5, 13) * mm, "end": v(0.5, 13) * mm});
            skLineSegment(sketch, "E8.5.5.4", {"start": v(3.5, 10) * mm, "end": v(0.5, 10) * mm});
            skPoint(sketch, "E8.5.5.5", {"position": v(0.5, 13) * mm});
            skPoint(sketch, "E8.5.5.6", {"position": v(2, 11.5) * mm});
            skPoint(sketch, "E8.5.5.7", {"position": v(2, 11.5) * mm});
            skPoint(sketch, "E8.5.6.0", {"position": v(2, 6.9) * mm});
            skLineSegment(sketch, "E8.5.6.1", {"start": v(0.5, 5.4) * mm, "end": v(0.5, 8.4) * mm});
            skLineSegment(sketch, "E8.5.6.2", {"start": v(3.5, 5.4) * mm, "end": v(3.5, 8.4) * mm});
            skLineSegment(sketch, "E8.5.6.3", {"start": v(3.5, 8.4) * mm, "end": v(0.5, 8.4) * mm});
            skLineSegment(sketch, "E8.5.6.4", {"start": v(3.5, 5.4) * mm, "end": v(0.5, 5.4) * mm});
            skPoint(sketch, "E8.5.6.5", {"position": v(0.5, 8.4) * mm});
            skPoint(sketch, "E8.5.6.6", {"position": v(2, 6.9) * mm});
            skPoint(sketch, "E8.5.6.7", {"position": v(2, 6.9) * mm});
            skPoint(sketch, "E8.5.7.0", {"position": v(2, 2.3) * mm});
            skLineSegment(sketch, "E8.5.7.1", {"start": v(0.5, 0.8) * mm, "end": v(0.5, 3.8) * mm});
            skLineSegment(sketch, "E8.5.7.2", {"start": v(3.5, 0.8) * mm, "end": v(3.5, 3.8) * mm});
            skLineSegment(sketch, "E8.5.7.3", {"start": v(3.5, 3.8) * mm, "end": v(0.5, 3.8) * mm});
            skLineSegment(sketch, "E8.5.7.4", {"start": v(3.5, 0.8) * mm, "end": v(0.5, 0.8) * mm});
            skPoint(sketch, "E8.5.7.5", {"position": v(0.5, 3.8) * mm});
            skPoint(sketch, "E8.5.7.6", {"position": v(2, 2.3) * mm});
            skPoint(sketch, "E8.5.7.7", {"position": v(2, 2.3) * mm});
            skPoint(sketch, "E8.5.8.0", {"position": v(2, -2.3) * mm});
            skLineSegment(sketch, "E8.5.8.1", {"start": v(0.5, -3.8) * mm, "end": v(0.5, -0.8) * mm});
            skLineSegment(sketch, "E8.5.8.2", {"start": v(3.5, -3.8) * mm, "end": v(3.5, -0.8) * mm});
            skLineSegment(sketch, "E8.5.8.3", {"start": v(3.5, -0.8) * mm, "end": v(0.5, -0.8) * mm});
            skLineSegment(sketch, "E8.5.8.4", {"start": v(3.5, -3.8) * mm, "end": v(0.5, -3.8) * mm});
            skPoint(sketch, "E8.5.8.5", {"position": v(0.5, -0.8) * mm});
            skPoint(sketch, "E8.5.8.6", {"position": v(2, -2.3) * mm});
            skPoint(sketch, "E8.5.8.7", {"position": v(2, -2.3) * mm});
            skPoint(sketch, "E8.5.9.0", {"position": v(2, -6.9) * mm});
            skLineSegment(sketch, "E8.5.9.1", {"start": v(0.5, -8.4) * mm, "end": v(0.5, -5.4) * mm});
            skLineSegment(sketch, "E8.5.9.2", {"start": v(3.5, -8.4) * mm, "end": v(3.5, -5.4) * mm});
            skLineSegment(sketch, "E8.5.9.3", {"start": v(3.5, -5.4) * mm, "end": v(0.5, -5.4) * mm});
            skLineSegment(sketch, "E8.5.9.4", {"start": v(3.5, -8.4) * mm, "end": v(0.5, -8.4) * mm});
            skPoint(sketch, "E8.5.9.5", {"position": v(0.5, -5.4) * mm});
            skPoint(sketch, "E8.5.9.6", {"position": v(2, -6.9) * mm});
            skPoint(sketch, "E8.5.9.7", {"position": v(2, -6.9) * mm});
            skPoint(sketch, "E8.5.10.0", {"position": v(2, -11.5) * mm});
            skLineSegment(sketch, "E8.5.10.1", {"start": v(0.5, -13) * mm, "end": v(0.5, -10) * mm});
            skLineSegment(sketch, "E8.5.10.2", {"start": v(3.5, -13) * mm, "end": v(3.5, -10) * mm});
            skLineSegment(sketch, "E8.5.10.3", {"start": v(3.5, -10) * mm, "end": v(0.5, -10) * mm});
            skLineSegment(sketch, "E8.5.10.4", {"start": v(3.5, -13) * mm, "end": v(0.5, -13) * mm});
            skPoint(sketch, "E8.5.10.5", {"position": v(0.5, -10) * mm});
            skPoint(sketch, "E8.5.10.6", {"position": v(2, -11.5) * mm});
            skPoint(sketch, "E8.5.10.7", {"position": v(2, -11.5) * mm});
            skPoint(sketch, "E8.5.11.0", {"position": v(2, -16.1) * mm});
            skLineSegment(sketch, "E8.5.11.1", {"start": v(0.5, -17.6) * mm, "end": v(0.5, -14.6) * mm});
            skLineSegment(sketch, "E8.5.11.2", {"start": v(3.5, -17.6) * mm, "end": v(3.5, -14.6) * mm});
            skLineSegment(sketch, "E8.5.11.3", {"start": v(3.5, -14.6) * mm, "end": v(0.5, -14.6) * mm});
            skLineSegment(sketch, "E8.5.11.4", {"start": v(3.5, -17.6) * mm, "end": v(0.5, -17.6) * mm});
            skPoint(sketch, "E8.5.11.5", {"position": v(0.5, -14.6) * mm});
            skPoint(sketch, "E8.5.11.6", {"position": v(2, -16.1) * mm});
            skPoint(sketch, "E8.5.11.7", {"position": v(2, -16.1) * mm});
            skPoint(sketch, "E8.5.12.0", {"position": v(2, -20.7) * mm});
            skLineSegment(sketch, "E8.5.12.1", {"start": v(0.5, -22.2) * mm, "end": v(0.5, -19.2) * mm});
            skLineSegment(sketch, "E8.5.12.2", {"start": v(3.5, -22.2) * mm, "end": v(3.5, -19.2) * mm});
            skLineSegment(sketch, "E8.5.12.3", {"start": v(3.5, -19.2) * mm, "end": v(0.5, -19.2) * mm});
            skLineSegment(sketch, "E8.5.12.4", {"start": v(3.5, -22.2) * mm, "end": v(0.5, -22.2) * mm});
            skPoint(sketch, "E8.5.12.5", {"position": v(0.5, -19.2) * mm});
            skPoint(sketch, "E8.5.12.6", {"position": v(2, -20.7) * mm});
            skPoint(sketch, "E8.5.12.7", {"position": v(2, -20.7) * mm});
            skPoint(sketch, "E8.5.13.0", {"position": v(2, -25.3) * mm});
            skLineSegment(sketch, "E8.5.13.1", {"start": v(0.5, -26.8) * mm, "end": v(0.5, -23.8) * mm});
            skLineSegment(sketch, "E8.5.13.2", {"start": v(3.5, -26.8) * mm, "end": v(3.5, -23.8) * mm});
            skLineSegment(sketch, "E8.5.13.3", {"start": v(3.5, -23.8) * mm, "end": v(0.5, -23.8) * mm});
            skLineSegment(sketch, "E8.5.13.4", {"start": v(3.5, -26.8) * mm, "end": v(0.5, -26.8) * mm});
            skPoint(sketch, "E8.5.13.5", {"position": v(0.5, -23.8) * mm});
            skPoint(sketch, "E8.5.13.6", {"position": v(2, -25.3) * mm});
            skPoint(sketch, "E8.5.13.7", {"position": v(2, -25.3) * mm});
            skPoint(sketch, "E8.5.14.0", {"position": v(2, -29.9) * mm});
            skLineSegment(sketch, "E8.5.14.1", {"start": v(0.5, -31.4) * mm, "end": v(0.5, -28.4) * mm});
            skLineSegment(sketch, "E8.5.14.2", {"start": v(3.5, -31.4) * mm, "end": v(3.5, -28.4) * mm});
            skLineSegment(sketch, "E8.5.14.3", {"start": v(3.5, -28.4) * mm, "end": v(0.5, -28.4) * mm});
            skLineSegment(sketch, "E8.5.14.4", {"start": v(3.5, -31.4) * mm, "end": v(0.5, -31.4) * mm});
            skPoint(sketch, "E8.5.14.5", {"position": v(0.5, -28.4) * mm});
            skPoint(sketch, "E8.5.14.6", {"position": v(2, -29.9) * mm});
            skPoint(sketch, "E8.5.14.7", {"position": v(2, -29.9) * mm});
            skPoint(sketch, "E8.5.15.0", {"position": v(2, -34.5) * mm});
            skLineSegment(sketch, "E8.5.15.1", {"start": v(0.5, -36) * mm, "end": v(0.5, -33) * mm});
            skLineSegment(sketch, "E8.5.15.2", {"start": v(3.5, -36) * mm, "end": v(3.5, -33) * mm});
            skLineSegment(sketch, "E8.5.15.3", {"start": v(3.5, -33) * mm, "end": v(0.5, -33) * mm});
            skLineSegment(sketch, "E8.5.15.4", {"start": v(3.5, -36) * mm, "end": v(0.5, -36) * mm});
            skPoint(sketch, "E8.5.15.5", {"position": v(0.5, -33) * mm});
            skPoint(sketch, "E8.5.15.6", {"position": v(2, -34.5) * mm});
            skPoint(sketch, "E8.5.15.7", {"position": v(2, -34.5) * mm});
            skPoint(sketch, "E8.6.0.0", {"position": v(6.5, 34.5) * mm});
            skLineSegment(sketch, "E8.6.0.1", {"start": v(5, 33) * mm, "end": v(5, 36) * mm});
            skLineSegment(sketch, "E8.6.0.2", {"start": v(8, 33) * mm, "end": v(8, 36) * mm});
            skLineSegment(sketch, "E8.6.0.3", {"start": v(8, 36) * mm, "end": v(5, 36) * mm});
            skLineSegment(sketch, "E8.6.0.4", {"start": v(8, 33) * mm, "end": v(5, 33) * mm});
            skPoint(sketch, "E8.6.0.5", {"position": v(5, 36) * mm});
            skPoint(sketch, "E8.6.0.6", {"position": v(6.5, 34.5) * mm});
            skPoint(sketch, "E8.6.0.7", {"position": v(6.5, 34.5) * mm});
            skPoint(sketch, "E8.6.1.0", {"position": v(6.5, 29.9) * mm});
            skLineSegment(sketch, "E8.6.1.1", {"start": v(5, 28.4) * mm, "end": v(5, 31.4) * mm});
            skLineSegment(sketch, "E8.6.1.2", {"start": v(8, 28.4) * mm, "end": v(8, 31.4) * mm});
            skLineSegment(sketch, "E8.6.1.3", {"start": v(8, 31.4) * mm, "end": v(5, 31.4) * mm});
            skLineSegment(sketch, "E8.6.1.4", {"start": v(8, 28.4) * mm, "end": v(5, 28.4) * mm});
            skPoint(sketch, "E8.6.1.5", {"position": v(5, 31.4) * mm});
            skPoint(sketch, "E8.6.1.6", {"position": v(6.5, 29.9) * mm});
            skPoint(sketch, "E8.6.1.7", {"position": v(6.5, 29.9) * mm});
            skPoint(sketch, "E8.6.2.0", {"position": v(6.5, 25.3) * mm});
            skLineSegment(sketch, "E8.6.2.1", {"start": v(5, 23.8) * mm, "end": v(5, 26.8) * mm});
            skLineSegment(sketch, "E8.6.2.2", {"start": v(8, 23.8) * mm, "end": v(8, 26.8) * mm});
            skLineSegment(sketch, "E8.6.2.3", {"start": v(8, 26.8) * mm, "end": v(5, 26.8) * mm});
            skLineSegment(sketch, "E8.6.2.4", {"start": v(8, 23.8) * mm, "end": v(5, 23.8) * mm});
            skPoint(sketch, "E8.6.2.5", {"position": v(5, 26.8) * mm});
            skPoint(sketch, "E8.6.2.6", {"position": v(6.5, 25.3) * mm});
            skPoint(sketch, "E8.6.2.7", {"position": v(6.5, 25.3) * mm});
            skPoint(sketch, "E8.6.3.0", {"position": v(6.5, 20.7) * mm});
            skLineSegment(sketch, "E8.6.3.1", {"start": v(5, 19.2) * mm, "end": v(5, 22.2) * mm});
            skLineSegment(sketch, "E8.6.3.2", {"start": v(8, 19.2) * mm, "end": v(8, 22.2) * mm});
            skLineSegment(sketch, "E8.6.3.3", {"start": v(8, 22.2) * mm, "end": v(5, 22.2) * mm});
            skLineSegment(sketch, "E8.6.3.4", {"start": v(8, 19.2) * mm, "end": v(5, 19.2) * mm});
            skPoint(sketch, "E8.6.3.5", {"position": v(5, 22.2) * mm});
            skPoint(sketch, "E8.6.3.6", {"position": v(6.5, 20.7) * mm});
            skPoint(sketch, "E8.6.3.7", {"position": v(6.5, 20.7) * mm});
            skPoint(sketch, "E8.6.4.0", {"position": v(6.5, 16.1) * mm});
            skLineSegment(sketch, "E8.6.4.1", {"start": v(5, 14.6) * mm, "end": v(5, 17.6) * mm});
            skLineSegment(sketch, "E8.6.4.2", {"start": v(8, 14.6) * mm, "end": v(8, 17.6) * mm});
            skLineSegment(sketch, "E8.6.4.3", {"start": v(8, 17.6) * mm, "end": v(5, 17.6) * mm});
            skLineSegment(sketch, "E8.6.4.4", {"start": v(8, 14.6) * mm, "end": v(5, 14.6) * mm});
            skPoint(sketch, "E8.6.4.5", {"position": v(5, 17.6) * mm});
            skPoint(sketch, "E8.6.4.6", {"position": v(6.5, 16.1) * mm});
            skPoint(sketch, "E8.6.4.7", {"position": v(6.5, 16.1) * mm});
            skPoint(sketch, "E8.6.5.0", {"position": v(6.5, 11.5) * mm});
            skLineSegment(sketch, "E8.6.5.1", {"start": v(5, 10) * mm, "end": v(5, 13) * mm});
            skLineSegment(sketch, "E8.6.5.2", {"start": v(8, 10) * mm, "end": v(8, 13) * mm});
            skLineSegment(sketch, "E8.6.5.3", {"start": v(8, 13) * mm, "end": v(5, 13) * mm});
            skLineSegment(sketch, "E8.6.5.4", {"start": v(8, 10) * mm, "end": v(5, 10) * mm});
            skPoint(sketch, "E8.6.5.5", {"position": v(5, 13) * mm});
            skPoint(sketch, "E8.6.5.6", {"position": v(6.5, 11.5) * mm});
            skPoint(sketch, "E8.6.5.7", {"position": v(6.5, 11.5) * mm});
            skPoint(sketch, "E8.6.6.0", {"position": v(6.5, 6.9) * mm});
            skLineSegment(sketch, "E8.6.6.1", {"start": v(5, 5.4) * mm, "end": v(5, 8.4) * mm});
            skLineSegment(sketch, "E8.6.6.2", {"start": v(8, 5.4) * mm, "end": v(8, 8.4) * mm});
            skLineSegment(sketch, "E8.6.6.3", {"start": v(8, 8.4) * mm, "end": v(5, 8.4) * mm});
            skLineSegment(sketch, "E8.6.6.4", {"start": v(8, 5.4) * mm, "end": v(5, 5.4) * mm});
            skPoint(sketch, "E8.6.6.5", {"position": v(5, 8.4) * mm});
            skPoint(sketch, "E8.6.6.6", {"position": v(6.5, 6.9) * mm});
            skPoint(sketch, "E8.6.6.7", {"position": v(6.5, 6.9) * mm});
            skPoint(sketch, "E8.6.7.0", {"position": v(6.5, 2.3) * mm});
            skLineSegment(sketch, "E8.6.7.1", {"start": v(5, 0.8) * mm, "end": v(5, 3.8) * mm});
            skLineSegment(sketch, "E8.6.7.2", {"start": v(8, 0.8) * mm, "end": v(8, 3.8) * mm});
            skLineSegment(sketch, "E8.6.7.3", {"start": v(8, 3.8) * mm, "end": v(5, 3.8) * mm});
            skLineSegment(sketch, "E8.6.7.4", {"start": v(8, 0.8) * mm, "end": v(5, 0.8) * mm});
            skPoint(sketch, "E8.6.7.5", {"position": v(5, 3.8) * mm});
            skPoint(sketch, "E8.6.7.6", {"position": v(6.5, 2.3) * mm});
            skPoint(sketch, "E8.6.7.7", {"position": v(6.5, 2.3) * mm});
            skPoint(sketch, "E8.6.8.0", {"position": v(6.5, -2.3) * mm});
            skLineSegment(sketch, "E8.6.8.1", {"start": v(5, -3.8) * mm, "end": v(5, -0.8) * mm});
            skLineSegment(sketch, "E8.6.8.2", {"start": v(8, -3.8) * mm, "end": v(8, -0.8) * mm});
            skLineSegment(sketch, "E8.6.8.3", {"start": v(8, -0.8) * mm, "end": v(5, -0.8) * mm});
            skLineSegment(sketch, "E8.6.8.4", {"start": v(8, -3.8) * mm, "end": v(5, -3.8) * mm});
            skPoint(sketch, "E8.6.8.5", {"position": v(5, -0.8) * mm});
            skPoint(sketch, "E8.6.8.6", {"position": v(6.5, -2.3) * mm});
            skPoint(sketch, "E8.6.8.7", {"position": v(6.5, -2.3) * mm});
            skPoint(sketch, "E8.6.9.0", {"position": v(6.5, -6.9) * mm});
            skLineSegment(sketch, "E8.6.9.1", {"start": v(5, -8.4) * mm, "end": v(5, -5.4) * mm});
            skLineSegment(sketch, "E8.6.9.2", {"start": v(8, -8.4) * mm, "end": v(8, -5.4) * mm});
            skLineSegment(sketch, "E8.6.9.3", {"start": v(8, -5.4) * mm, "end": v(5, -5.4) * mm});
            skLineSegment(sketch, "E8.6.9.4", {"start": v(8, -8.4) * mm, "end": v(5, -8.4) * mm});
            skPoint(sketch, "E8.6.9.5", {"position": v(5, -5.4) * mm});
            skPoint(sketch, "E8.6.9.6", {"position": v(6.5, -6.9) * mm});
            skPoint(sketch, "E8.6.9.7", {"position": v(6.5, -6.9) * mm});
            skPoint(sketch, "E8.6.10.0", {"position": v(6.5, -11.5) * mm});
            skLineSegment(sketch, "E8.6.10.1", {"start": v(5, -13) * mm, "end": v(5, -10) * mm});
            skLineSegment(sketch, "E8.6.10.2", {"start": v(8, -13) * mm, "end": v(8, -10) * mm});
            skLineSegment(sketch, "E8.6.10.3", {"start": v(8, -10) * mm, "end": v(5, -10) * mm});
            skLineSegment(sketch, "E8.6.10.4", {"start": v(8, -13) * mm, "end": v(5, -13) * mm});
            skPoint(sketch, "E8.6.10.5", {"position": v(5, -10) * mm});
            skPoint(sketch, "E8.6.10.6", {"position": v(6.5, -11.5) * mm});
            skPoint(sketch, "E8.6.10.7", {"position": v(6.5, -11.5) * mm});
            skPoint(sketch, "E8.6.11.0", {"position": v(6.5, -16.1) * mm});
            skLineSegment(sketch, "E8.6.11.1", {"start": v(5, -17.6) * mm, "end": v(5, -14.6) * mm});
            skLineSegment(sketch, "E8.6.11.2", {"start": v(8, -17.6) * mm, "end": v(8, -14.6) * mm});
            skLineSegment(sketch, "E8.6.11.3", {"start": v(8, -14.6) * mm, "end": v(5, -14.6) * mm});
            skLineSegment(sketch, "E8.6.11.4", {"start": v(8, -17.6) * mm, "end": v(5, -17.6) * mm});
            skPoint(sketch, "E8.6.11.5", {"position": v(5, -14.6) * mm});
            skPoint(sketch, "E8.6.11.6", {"position": v(6.5, -16.1) * mm});
            skPoint(sketch, "E8.6.11.7", {"position": v(6.5, -16.1) * mm});
            skPoint(sketch, "E8.6.12.0", {"position": v(6.5, -20.7) * mm});
            skLineSegment(sketch, "E8.6.12.1", {"start": v(5, -22.2) * mm, "end": v(5, -19.2) * mm});
            skLineSegment(sketch, "E8.6.12.2", {"start": v(8, -22.2) * mm, "end": v(8, -19.2) * mm});
            skLineSegment(sketch, "E8.6.12.3", {"start": v(8, -19.2) * mm, "end": v(5, -19.2) * mm});
            skLineSegment(sketch, "E8.6.12.4", {"start": v(8, -22.2) * mm, "end": v(5, -22.2) * mm});
            skPoint(sketch, "E8.6.12.5", {"position": v(5, -19.2) * mm});
            skPoint(sketch, "E8.6.12.6", {"position": v(6.5, -20.7) * mm});
            skPoint(sketch, "E8.6.12.7", {"position": v(6.5, -20.7) * mm});
            skPoint(sketch, "E8.6.13.0", {"position": v(6.5, -25.3) * mm});
            skLineSegment(sketch, "E8.6.13.1", {"start": v(5, -26.8) * mm, "end": v(5, -23.8) * mm});
            skLineSegment(sketch, "E8.6.13.2", {"start": v(8, -26.8) * mm, "end": v(8, -23.8) * mm});
            skLineSegment(sketch, "E8.6.13.3", {"start": v(8, -23.8) * mm, "end": v(5, -23.8) * mm});
            skLineSegment(sketch, "E8.6.13.4", {"start": v(8, -26.8) * mm, "end": v(5, -26.8) * mm});
            skPoint(sketch, "E8.6.13.5", {"position": v(5, -23.8) * mm});
            skPoint(sketch, "E8.6.13.6", {"position": v(6.5, -25.3) * mm});
            skPoint(sketch, "E8.6.13.7", {"position": v(6.5, -25.3) * mm});
            skPoint(sketch, "E8.6.14.0", {"position": v(6.5, -29.9) * mm});
            skLineSegment(sketch, "E8.6.14.1", {"start": v(5, -31.4) * mm, "end": v(5, -28.4) * mm});
            skLineSegment(sketch, "E8.6.14.2", {"start": v(8, -31.4) * mm, "end": v(8, -28.4) * mm});
            skLineSegment(sketch, "E8.6.14.3", {"start": v(8, -28.4) * mm, "end": v(5, -28.4) * mm});
            skLineSegment(sketch, "E8.6.14.4", {"start": v(8, -31.4) * mm, "end": v(5, -31.4) * mm});
            skPoint(sketch, "E8.6.14.5", {"position": v(5, -28.4) * mm});
            skPoint(sketch, "E8.6.14.6", {"position": v(6.5, -29.9) * mm});
            skPoint(sketch, "E8.6.14.7", {"position": v(6.5, -29.9) * mm});
            skPoint(sketch, "E8.6.15.0", {"position": v(6.5, -34.5) * mm});
            skLineSegment(sketch, "E8.6.15.1", {"start": v(5, -36) * mm, "end": v(5, -33) * mm});
            skLineSegment(sketch, "E8.6.15.2", {"start": v(8, -36) * mm, "end": v(8, -33) * mm});
            skLineSegment(sketch, "E8.6.15.3", {"start": v(8, -33) * mm, "end": v(5, -33) * mm});
            skLineSegment(sketch, "E8.6.15.4", {"start": v(8, -36) * mm, "end": v(5, -36) * mm});
            skPoint(sketch, "E8.6.15.5", {"position": v(5, -33) * mm});
            skPoint(sketch, "E8.6.15.6", {"position": v(6.5, -34.5) * mm});
            skPoint(sketch, "E8.6.15.7", {"position": v(6.5, -34.5) * mm});
            skPoint(sketch, "E8.7.0.0", {"position": v(11, 34.5) * mm});
            skLineSegment(sketch, "E8.7.0.1", {"start": v(9.5, 33) * mm, "end": v(9.5, 36) * mm});
            skLineSegment(sketch, "E8.7.0.2", {"start": v(12.5, 33) * mm, "end": v(12.5, 36) * mm});
            skLineSegment(sketch, "E8.7.0.3", {"start": v(12.5, 36) * mm, "end": v(9.5, 36) * mm});
            skLineSegment(sketch, "E8.7.0.4", {"start": v(12.5, 33) * mm, "end": v(9.5, 33) * mm});
            skPoint(sketch, "E8.7.0.5", {"position": v(9.5, 36) * mm});
            skPoint(sketch, "E8.7.0.6", {"position": v(11, 34.5) * mm});
            skPoint(sketch, "E8.7.0.7", {"position": v(11, 34.5) * mm});
            skPoint(sketch, "E8.7.1.0", {"position": v(11, 29.9) * mm});
            skLineSegment(sketch, "E8.7.1.1", {"start": v(9.5, 28.4) * mm, "end": v(9.5, 31.4) * mm});
            skLineSegment(sketch, "E8.7.1.2", {"start": v(12.5, 28.4) * mm, "end": v(12.5, 31.4) * mm});
            skLineSegment(sketch, "E8.7.1.3", {"start": v(12.5, 31.4) * mm, "end": v(9.5, 31.4) * mm});
            skLineSegment(sketch, "E8.7.1.4", {"start": v(12.5, 28.4) * mm, "end": v(9.5, 28.4) * mm});
            skPoint(sketch, "E8.7.1.5", {"position": v(9.5, 31.4) * mm});
            skPoint(sketch, "E8.7.1.6", {"position": v(11, 29.9) * mm});
            skPoint(sketch, "E8.7.1.7", {"position": v(11, 29.9) * mm});
            skPoint(sketch, "E8.7.2.0", {"position": v(11, 25.3) * mm});
            skLineSegment(sketch, "E8.7.2.1", {"start": v(9.5, 23.8) * mm, "end": v(9.5, 26.8) * mm});
            skLineSegment(sketch, "E8.7.2.2", {"start": v(12.5, 23.8) * mm, "end": v(12.5, 26.8) * mm});
            skLineSegment(sketch, "E8.7.2.3", {"start": v(12.5, 26.8) * mm, "end": v(9.5, 26.8) * mm});
            skLineSegment(sketch, "E8.7.2.4", {"start": v(12.5, 23.8) * mm, "end": v(9.5, 23.8) * mm});
            skPoint(sketch, "E8.7.2.5", {"position": v(9.5, 26.8) * mm});
            skPoint(sketch, "E8.7.2.6", {"position": v(11, 25.3) * mm});
            skPoint(sketch, "E8.7.2.7", {"position": v(11, 25.3) * mm});
            skPoint(sketch, "E8.7.3.0", {"position": v(11, 20.7) * mm});
            skLineSegment(sketch, "E8.7.3.1", {"start": v(9.5, 19.2) * mm, "end": v(9.5, 22.2) * mm});
            skLineSegment(sketch, "E8.7.3.2", {"start": v(12.5, 19.2) * mm, "end": v(12.5, 22.2) * mm});
            skLineSegment(sketch, "E8.7.3.3", {"start": v(12.5, 22.2) * mm, "end": v(9.5, 22.2) * mm});
            skLineSegment(sketch, "E8.7.3.4", {"start": v(12.5, 19.2) * mm, "end": v(9.5, 19.2) * mm});
            skPoint(sketch, "E8.7.3.5", {"position": v(9.5, 22.2) * mm});
            skPoint(sketch, "E8.7.3.6", {"position": v(11, 20.7) * mm});
            skPoint(sketch, "E8.7.3.7", {"position": v(11, 20.7) * mm});
            skPoint(sketch, "E8.7.4.0", {"position": v(11, 16.1) * mm});
            skLineSegment(sketch, "E8.7.4.1", {"start": v(9.5, 14.6) * mm, "end": v(9.5, 17.6) * mm});
            skLineSegment(sketch, "E8.7.4.2", {"start": v(12.5, 14.6) * mm, "end": v(12.5, 17.6) * mm});
            skLineSegment(sketch, "E8.7.4.3", {"start": v(12.5, 17.6) * mm, "end": v(9.5, 17.6) * mm});
            skLineSegment(sketch, "E8.7.4.4", {"start": v(12.5, 14.6) * mm, "end": v(9.5, 14.6) * mm});
            skPoint(sketch, "E8.7.4.5", {"position": v(9.5, 17.6) * mm});
            skPoint(sketch, "E8.7.4.6", {"position": v(11, 16.1) * mm});
            skPoint(sketch, "E8.7.4.7", {"position": v(11, 16.1) * mm});
            skPoint(sketch, "E8.7.5.0", {"position": v(11, 11.5) * mm});
            skLineSegment(sketch, "E8.7.5.1", {"start": v(9.5, 10) * mm, "end": v(9.5, 13) * mm});
            skLineSegment(sketch, "E8.7.5.2", {"start": v(12.5, 10) * mm, "end": v(12.5, 13) * mm});
            skLineSegment(sketch, "E8.7.5.3", {"start": v(12.5, 13) * mm, "end": v(9.5, 13) * mm});
            skLineSegment(sketch, "E8.7.5.4", {"start": v(12.5, 10) * mm, "end": v(9.5, 10) * mm});
            skPoint(sketch, "E8.7.5.5", {"position": v(9.5, 13) * mm});
            skPoint(sketch, "E8.7.5.6", {"position": v(11, 11.5) * mm});
            skPoint(sketch, "E8.7.5.7", {"position": v(11, 11.5) * mm});
            skPoint(sketch, "E8.7.6.0", {"position": v(11, 6.9) * mm});
            skLineSegment(sketch, "E8.7.6.1", {"start": v(9.5, 5.4) * mm, "end": v(9.5, 8.4) * mm});
            skLineSegment(sketch, "E8.7.6.2", {"start": v(12.5, 5.4) * mm, "end": v(12.5, 8.4) * mm});
            skLineSegment(sketch, "E8.7.6.3", {"start": v(12.5, 8.4) * mm, "end": v(9.5, 8.4) * mm});
            skLineSegment(sketch, "E8.7.6.4", {"start": v(12.5, 5.4) * mm, "end": v(9.5, 5.4) * mm});
            skPoint(sketch, "E8.7.6.5", {"position": v(9.5, 8.4) * mm});
            skPoint(sketch, "E8.7.6.6", {"position": v(11, 6.9) * mm});
            skPoint(sketch, "E8.7.6.7", {"position": v(11, 6.9) * mm});
            skPoint(sketch, "E8.7.7.0", {"position": v(11, 2.3) * mm});
            skLineSegment(sketch, "E8.7.7.1", {"start": v(9.5, 0.8) * mm, "end": v(9.5, 3.8) * mm});
            skLineSegment(sketch, "E8.7.7.2", {"start": v(12.5, 0.8) * mm, "end": v(12.5, 3.8) * mm});
            skLineSegment(sketch, "E8.7.7.3", {"start": v(12.5, 3.8) * mm, "end": v(9.5, 3.8) * mm});
            skLineSegment(sketch, "E8.7.7.4", {"start": v(12.5, 0.8) * mm, "end": v(9.5, 0.8) * mm});
            skPoint(sketch, "E8.7.7.5", {"position": v(9.5, 3.8) * mm});
            skPoint(sketch, "E8.7.7.6", {"position": v(11, 2.3) * mm});
            skPoint(sketch, "E8.7.7.7", {"position": v(11, 2.3) * mm});
            skPoint(sketch, "E8.7.8.0", {"position": v(11, -2.3) * mm});
            skLineSegment(sketch, "E8.7.8.1", {"start": v(9.5, -3.8) * mm, "end": v(9.5, -0.8) * mm});
            skLineSegment(sketch, "E8.7.8.2", {"start": v(12.5, -3.8) * mm, "end": v(12.5, -0.8) * mm});
            skLineSegment(sketch, "E8.7.8.3", {"start": v(12.5, -0.8) * mm, "end": v(9.5, -0.8) * mm});
            skLineSegment(sketch, "E8.7.8.4", {"start": v(12.5, -3.8) * mm, "end": v(9.5, -3.8) * mm});
            skPoint(sketch, "E8.7.8.5", {"position": v(9.5, -0.8) * mm});
            skPoint(sketch, "E8.7.8.6", {"position": v(11, -2.3) * mm});
            skPoint(sketch, "E8.7.8.7", {"position": v(11, -2.3) * mm});
            skPoint(sketch, "E8.7.9.0", {"position": v(11, -6.9) * mm});
            skLineSegment(sketch, "E8.7.9.1", {"start": v(9.5, -8.4) * mm, "end": v(9.5, -5.4) * mm});
            skLineSegment(sketch, "E8.7.9.2", {"start": v(12.5, -8.4) * mm, "end": v(12.5, -5.4) * mm});
            skLineSegment(sketch, "E8.7.9.3", {"start": v(12.5, -5.4) * mm, "end": v(9.5, -5.4) * mm});
            skLineSegment(sketch, "E8.7.9.4", {"start": v(12.5, -8.4) * mm, "end": v(9.5, -8.4) * mm});
            skPoint(sketch, "E8.7.9.5", {"position": v(9.5, -5.4) * mm});
            skPoint(sketch, "E8.7.9.6", {"position": v(11, -6.9) * mm});
            skPoint(sketch, "E8.7.9.7", {"position": v(11, -6.9) * mm});
            skPoint(sketch, "E8.7.10.0", {"position": v(11, -11.5) * mm});
            skLineSegment(sketch, "E8.7.10.1", {"start": v(9.5, -13) * mm, "end": v(9.5, -10) * mm});
            skLineSegment(sketch, "E8.7.10.2", {"start": v(12.5, -13) * mm, "end": v(12.5, -10) * mm});
            skLineSegment(sketch, "E8.7.10.3", {"start": v(12.5, -10) * mm, "end": v(9.5, -10) * mm});
            skLineSegment(sketch, "E8.7.10.4", {"start": v(12.5, -13) * mm, "end": v(9.5, -13) * mm});
            skPoint(sketch, "E8.7.10.5", {"position": v(9.5, -10) * mm});
            skPoint(sketch, "E8.7.10.6", {"position": v(11, -11.5) * mm});
            skPoint(sketch, "E8.7.10.7", {"position": v(11, -11.5) * mm});
            skPoint(sketch, "E8.7.11.0", {"position": v(11, -16.1) * mm});
            skLineSegment(sketch, "E8.7.11.1", {"start": v(9.5, -17.6) * mm, "end": v(9.5, -14.6) * mm});
            skLineSegment(sketch, "E8.7.11.2", {"start": v(12.5, -17.6) * mm, "end": v(12.5, -14.6) * mm});
            skLineSegment(sketch, "E8.7.11.3", {"start": v(12.5, -14.6) * mm, "end": v(9.5, -14.6) * mm});
            skLineSegment(sketch, "E8.7.11.4", {"start": v(12.5, -17.6) * mm, "end": v(9.5, -17.6) * mm});
            skPoint(sketch, "E8.7.11.5", {"position": v(9.5, -14.6) * mm});
            skPoint(sketch, "E8.7.11.6", {"position": v(11, -16.1) * mm});
            skPoint(sketch, "E8.7.11.7", {"position": v(11, -16.1) * mm});
            skPoint(sketch, "E8.7.12.0", {"position": v(11, -20.7) * mm});
            skLineSegment(sketch, "E8.7.12.1", {"start": v(9.5, -22.2) * mm, "end": v(9.5, -19.2) * mm});
            skLineSegment(sketch, "E8.7.12.2", {"start": v(12.5, -22.2) * mm, "end": v(12.5, -19.2) * mm});
            skLineSegment(sketch, "E8.7.12.3", {"start": v(12.5, -19.2) * mm, "end": v(9.5, -19.2) * mm});
            skLineSegment(sketch, "E8.7.12.4", {"start": v(12.5, -22.2) * mm, "end": v(9.5, -22.2) * mm});
            skPoint(sketch, "E8.7.12.5", {"position": v(9.5, -19.2) * mm});
            skPoint(sketch, "E8.7.12.6", {"position": v(11, -20.7) * mm});
            skPoint(sketch, "E8.7.12.7", {"position": v(11, -20.7) * mm});
            skPoint(sketch, "E8.7.13.0", {"position": v(11, -25.3) * mm});
            skLineSegment(sketch, "E8.7.13.1", {"start": v(9.5, -26.8) * mm, "end": v(9.5, -23.8) * mm});
            skLineSegment(sketch, "E8.7.13.2", {"start": v(12.5, -26.8) * mm, "end": v(12.5, -23.8) * mm});
            skLineSegment(sketch, "E8.7.13.3", {"start": v(12.5, -23.8) * mm, "end": v(9.5, -23.8) * mm});
            skLineSegment(sketch, "E8.7.13.4", {"start": v(12.5, -26.8) * mm, "end": v(9.5, -26.8) * mm});
            skPoint(sketch, "E8.7.13.5", {"position": v(9.5, -23.8) * mm});
            skPoint(sketch, "E8.7.13.6", {"position": v(11, -25.3) * mm});
            skPoint(sketch, "E8.7.13.7", {"position": v(11, -25.3) * mm});
            skPoint(sketch, "E8.7.14.0", {"position": v(11, -29.9) * mm});
            skLineSegment(sketch, "E8.7.14.1", {"start": v(9.5, -31.4) * mm, "end": v(9.5, -28.4) * mm});
            skLineSegment(sketch, "E8.7.14.2", {"start": v(12.5, -31.4) * mm, "end": v(12.5, -28.4) * mm});
            skLineSegment(sketch, "E8.7.14.3", {"start": v(12.5, -28.4) * mm, "end": v(9.5, -28.4) * mm});
            skLineSegment(sketch, "E8.7.14.4", {"start": v(12.5, -31.4) * mm, "end": v(9.5, -31.4) * mm});
            skPoint(sketch, "E8.7.14.5", {"position": v(9.5, -28.4) * mm});
            skPoint(sketch, "E8.7.14.6", {"position": v(11, -29.9) * mm});
            skPoint(sketch, "E8.7.14.7", {"position": v(11, -29.9) * mm});
            skPoint(sketch, "E8.7.15.0", {"position": v(11, -34.5) * mm});
            skLineSegment(sketch, "E8.7.15.1", {"start": v(9.5, -36) * mm, "end": v(9.5, -33) * mm});
            skLineSegment(sketch, "E8.7.15.2", {"start": v(12.5, -36) * mm, "end": v(12.5, -33) * mm});
            skLineSegment(sketch, "E8.7.15.3", {"start": v(12.5, -33) * mm, "end": v(9.5, -33) * mm});
            skLineSegment(sketch, "E8.7.15.4", {"start": v(12.5, -36) * mm, "end": v(9.5, -36) * mm});
            skPoint(sketch, "E8.7.15.5", {"position": v(9.5, -33) * mm});
            skPoint(sketch, "E8.7.15.6", {"position": v(11, -34.5) * mm});
            skPoint(sketch, "E8.7.15.7", {"position": v(11, -34.5) * mm});
            skPoint(sketch, "E8.8.0.0", {"position": v(15.5, 34.5) * mm});
            skLineSegment(sketch, "E8.8.0.1", {"start": v(14, 33) * mm, "end": v(14, 36) * mm});
            skLineSegment(sketch, "E8.8.0.2", {"start": v(17, 33) * mm, "end": v(17, 36) * mm});
            skLineSegment(sketch, "E8.8.0.3", {"start": v(17, 36) * mm, "end": v(14, 36) * mm});
            skLineSegment(sketch, "E8.8.0.4", {"start": v(17, 33) * mm, "end": v(14, 33) * mm});
            skPoint(sketch, "E8.8.0.5", {"position": v(14, 36) * mm});
            skPoint(sketch, "E8.8.0.6", {"position": v(15.5, 34.5) * mm});
            skPoint(sketch, "E8.8.0.7", {"position": v(15.5, 34.5) * mm});
            skPoint(sketch, "E8.8.1.0", {"position": v(15.5, 29.9) * mm});
            skLineSegment(sketch, "E8.8.1.1", {"start": v(14, 28.4) * mm, "end": v(14, 31.4) * mm});
            skLineSegment(sketch, "E8.8.1.2", {"start": v(17, 28.4) * mm, "end": v(17, 31.4) * mm});
            skLineSegment(sketch, "E8.8.1.3", {"start": v(17, 31.4) * mm, "end": v(14, 31.4) * mm});
            skLineSegment(sketch, "E8.8.1.4", {"start": v(17, 28.4) * mm, "end": v(14, 28.4) * mm});
            skPoint(sketch, "E8.8.1.5", {"position": v(14, 31.4) * mm});
            skPoint(sketch, "E8.8.1.6", {"position": v(15.5, 29.9) * mm});
            skPoint(sketch, "E8.8.1.7", {"position": v(15.5, 29.9) * mm});
            skPoint(sketch, "E8.8.2.0", {"position": v(15.5, 25.3) * mm});
            skLineSegment(sketch, "E8.8.2.1", {"start": v(14, 23.8) * mm, "end": v(14, 26.8) * mm});
            skLineSegment(sketch, "E8.8.2.2", {"start": v(17, 23.8) * mm, "end": v(17, 26.8) * mm});
            skLineSegment(sketch, "E8.8.2.3", {"start": v(17, 26.8) * mm, "end": v(14, 26.8) * mm});
            skLineSegment(sketch, "E8.8.2.4", {"start": v(17, 23.8) * mm, "end": v(14, 23.8) * mm});
            skPoint(sketch, "E8.8.2.5", {"position": v(14, 26.8) * mm});
            skPoint(sketch, "E8.8.2.6", {"position": v(15.5, 25.3) * mm});
            skPoint(sketch, "E8.8.2.7", {"position": v(15.5, 25.3) * mm});
            skPoint(sketch, "E8.8.3.0", {"position": v(15.5, 20.7) * mm});
            skLineSegment(sketch, "E8.8.3.1", {"start": v(14, 19.2) * mm, "end": v(14, 22.2) * mm});
            skLineSegment(sketch, "E8.8.3.2", {"start": v(17, 19.2) * mm, "end": v(17, 22.2) * mm});
            skLineSegment(sketch, "E8.8.3.3", {"start": v(17, 22.2) * mm, "end": v(14, 22.2) * mm});
            skLineSegment(sketch, "E8.8.3.4", {"start": v(17, 19.2) * mm, "end": v(14, 19.2) * mm});
            skPoint(sketch, "E8.8.3.5", {"position": v(14, 22.2) * mm});
            skPoint(sketch, "E8.8.3.6", {"position": v(15.5, 20.7) * mm});
            skPoint(sketch, "E8.8.3.7", {"position": v(15.5, 20.7) * mm});
            skPoint(sketch, "E8.8.4.0", {"position": v(15.5, 16.1) * mm});
            skLineSegment(sketch, "E8.8.4.1", {"start": v(14, 14.6) * mm, "end": v(14, 17.6) * mm});
            skLineSegment(sketch, "E8.8.4.2", {"start": v(17, 14.6) * mm, "end": v(17, 17.6) * mm});
            skLineSegment(sketch, "E8.8.4.3", {"start": v(17, 17.6) * mm, "end": v(14, 17.6) * mm});
            skLineSegment(sketch, "E8.8.4.4", {"start": v(17, 14.6) * mm, "end": v(14, 14.6) * mm});
            skPoint(sketch, "E8.8.4.5", {"position": v(14, 17.6) * mm});
            skPoint(sketch, "E8.8.4.6", {"position": v(15.5, 16.1) * mm});
            skPoint(sketch, "E8.8.4.7", {"position": v(15.5, 16.1) * mm});
            skPoint(sketch, "E8.8.5.0", {"position": v(15.5, 11.5) * mm});
            skLineSegment(sketch, "E8.8.5.1", {"start": v(14, 10) * mm, "end": v(14, 13) * mm});
            skLineSegment(sketch, "E8.8.5.2", {"start": v(17, 10) * mm, "end": v(17, 13) * mm});
            skLineSegment(sketch, "E8.8.5.3", {"start": v(17, 13) * mm, "end": v(14, 13) * mm});
            skLineSegment(sketch, "E8.8.5.4", {"start": v(17, 10) * mm, "end": v(14, 10) * mm});
            skPoint(sketch, "E8.8.5.5", {"position": v(14, 13) * mm});
            skPoint(sketch, "E8.8.5.6", {"position": v(15.5, 11.5) * mm});
            skPoint(sketch, "E8.8.5.7", {"position": v(15.5, 11.5) * mm});
            skPoint(sketch, "E8.8.6.0", {"position": v(15.5, 6.9) * mm});
            skLineSegment(sketch, "E8.8.6.1", {"start": v(14, 5.4) * mm, "end": v(14, 8.4) * mm});
            skLineSegment(sketch, "E8.8.6.2", {"start": v(17, 5.4) * mm, "end": v(17, 8.4) * mm});
            skLineSegment(sketch, "E8.8.6.3", {"start": v(17, 8.4) * mm, "end": v(14, 8.4) * mm});
            skLineSegment(sketch, "E8.8.6.4", {"start": v(17, 5.4) * mm, "end": v(14, 5.4) * mm});
            skPoint(sketch, "E8.8.6.5", {"position": v(14, 8.4) * mm});
            skPoint(sketch, "E8.8.6.6", {"position": v(15.5, 6.9) * mm});
            skPoint(sketch, "E8.8.6.7", {"position": v(15.5, 6.9) * mm});
            skPoint(sketch, "E8.8.7.0", {"position": v(15.5, 2.3) * mm});
            skLineSegment(sketch, "E8.8.7.1", {"start": v(14, 0.8) * mm, "end": v(14, 3.8) * mm});
            skLineSegment(sketch, "E8.8.7.2", {"start": v(17, 0.8) * mm, "end": v(17, 3.8) * mm});
            skLineSegment(sketch, "E8.8.7.3", {"start": v(17, 3.8) * mm, "end": v(14, 3.8) * mm});
            skLineSegment(sketch, "E8.8.7.4", {"start": v(17, 0.8) * mm, "end": v(14, 0.8) * mm});
            skPoint(sketch, "E8.8.7.5", {"position": v(14, 3.8) * mm});
            skPoint(sketch, "E8.8.7.6", {"position": v(15.5, 2.3) * mm});
            skPoint(sketch, "E8.8.7.7", {"position": v(15.5, 2.3) * mm});
            skPoint(sketch, "E8.8.8.0", {"position": v(15.5, -2.3) * mm});
            skLineSegment(sketch, "E8.8.8.1", {"start": v(14, -3.8) * mm, "end": v(14, -0.8) * mm});
            skLineSegment(sketch, "E8.8.8.2", {"start": v(17, -3.8) * mm, "end": v(17, -0.8) * mm});
            skLineSegment(sketch, "E8.8.8.3", {"start": v(17, -0.8) * mm, "end": v(14, -0.8) * mm});
            skLineSegment(sketch, "E8.8.8.4", {"start": v(17, -3.8) * mm, "end": v(14, -3.8) * mm});
            skPoint(sketch, "E8.8.8.5", {"position": v(14, -0.8) * mm});
            skPoint(sketch, "E8.8.8.6", {"position": v(15.5, -2.3) * mm});
            skPoint(sketch, "E8.8.8.7", {"position": v(15.5, -2.3) * mm});
            skPoint(sketch, "E8.8.9.0", {"position": v(15.5, -6.9) * mm});
            skLineSegment(sketch, "E8.8.9.1", {"start": v(14, -8.4) * mm, "end": v(14, -5.4) * mm});
            skLineSegment(sketch, "E8.8.9.2", {"start": v(17, -8.4) * mm, "end": v(17, -5.4) * mm});
            skLineSegment(sketch, "E8.8.9.3", {"start": v(17, -5.4) * mm, "end": v(14, -5.4) * mm});
            skLineSegment(sketch, "E8.8.9.4", {"start": v(17, -8.4) * mm, "end": v(14, -8.4) * mm});
            skPoint(sketch, "E8.8.9.5", {"position": v(14, -5.4) * mm});
            skPoint(sketch, "E8.8.9.6", {"position": v(15.5, -6.9) * mm});
            skPoint(sketch, "E8.8.9.7", {"position": v(15.5, -6.9) * mm});
            skPoint(sketch, "E8.8.10.0", {"position": v(15.5, -11.5) * mm});
            skLineSegment(sketch, "E8.8.10.1", {"start": v(14, -13) * mm, "end": v(14, -10) * mm});
            skLineSegment(sketch, "E8.8.10.2", {"start": v(17, -13) * mm, "end": v(17, -10) * mm});
            skLineSegment(sketch, "E8.8.10.3", {"start": v(17, -10) * mm, "end": v(14, -10) * mm});
            skLineSegment(sketch, "E8.8.10.4", {"start": v(17, -13) * mm, "end": v(14, -13) * mm});
            skPoint(sketch, "E8.8.10.5", {"position": v(14, -10) * mm});
            skPoint(sketch, "E8.8.10.6", {"position": v(15.5, -11.5) * mm});
            skPoint(sketch, "E8.8.10.7", {"position": v(15.5, -11.5) * mm});
            skPoint(sketch, "E8.8.11.0", {"position": v(15.5, -16.1) * mm});
            skLineSegment(sketch, "E8.8.11.1", {"start": v(14, -17.6) * mm, "end": v(14, -14.6) * mm});
            skLineSegment(sketch, "E8.8.11.2", {"start": v(17, -17.6) * mm, "end": v(17, -14.6) * mm});
            skLineSegment(sketch, "E8.8.11.3", {"start": v(17, -14.6) * mm, "end": v(14, -14.6) * mm});
            skLineSegment(sketch, "E8.8.11.4", {"start": v(17, -17.6) * mm, "end": v(14, -17.6) * mm});
            skPoint(sketch, "E8.8.11.5", {"position": v(14, -14.6) * mm});
            skPoint(sketch, "E8.8.11.6", {"position": v(15.5, -16.1) * mm});
            skPoint(sketch, "E8.8.11.7", {"position": v(15.5, -16.1) * mm});
            skPoint(sketch, "E8.8.12.0", {"position": v(15.5, -20.7) * mm});
            skLineSegment(sketch, "E8.8.12.1", {"start": v(14, -22.2) * mm, "end": v(14, -19.2) * mm});
            skLineSegment(sketch, "E8.8.12.2", {"start": v(17, -22.2) * mm, "end": v(17, -19.2) * mm});
            skLineSegment(sketch, "E8.8.12.3", {"start": v(17, -19.2) * mm, "end": v(14, -19.2) * mm});
            skLineSegment(sketch, "E8.8.12.4", {"start": v(17, -22.2) * mm, "end": v(14, -22.2) * mm});
            skPoint(sketch, "E8.8.12.5", {"position": v(14, -19.2) * mm});
            skPoint(sketch, "E8.8.12.6", {"position": v(15.5, -20.7) * mm});
            skPoint(sketch, "E8.8.12.7", {"position": v(15.5, -20.7) * mm});
            skPoint(sketch, "E8.8.13.0", {"position": v(15.5, -25.3) * mm});
            skLineSegment(sketch, "E8.8.13.1", {"start": v(14, -26.8) * mm, "end": v(14, -23.8) * mm});
            skLineSegment(sketch, "E8.8.13.2", {"start": v(17, -26.8) * mm, "end": v(17, -23.8) * mm});
            skLineSegment(sketch, "E8.8.13.3", {"start": v(17, -23.8) * mm, "end": v(14, -23.8) * mm});
            skLineSegment(sketch, "E8.8.13.4", {"start": v(17, -26.8) * mm, "end": v(14, -26.8) * mm});
            skPoint(sketch, "E8.8.13.5", {"position": v(14, -23.8) * mm});
            skPoint(sketch, "E8.8.13.6", {"position": v(15.5, -25.3) * mm});
            skPoint(sketch, "E8.8.13.7", {"position": v(15.5, -25.3) * mm});
            skPoint(sketch, "E8.8.14.0", {"position": v(15.5, -29.9) * mm});
            skLineSegment(sketch, "E8.8.14.1", {"start": v(14, -31.4) * mm, "end": v(14, -28.4) * mm});
            skLineSegment(sketch, "E8.8.14.2", {"start": v(17, -31.4) * mm, "end": v(17, -28.4) * mm});
            skLineSegment(sketch, "E8.8.14.3", {"start": v(17, -28.4) * mm, "end": v(14, -28.4) * mm});
            skLineSegment(sketch, "E8.8.14.4", {"start": v(17, -31.4) * mm, "end": v(14, -31.4) * mm});
            skPoint(sketch, "E8.8.14.5", {"position": v(14, -28.4) * mm});
            skPoint(sketch, "E8.8.14.6", {"position": v(15.5, -29.9) * mm});
            skPoint(sketch, "E8.8.14.7", {"position": v(15.5, -29.9) * mm});
            skPoint(sketch, "E8.8.15.0", {"position": v(15.5, -34.5) * mm});
            skLineSegment(sketch, "E8.8.15.1", {"start": v(14, -36) * mm, "end": v(14, -33) * mm});
            skLineSegment(sketch, "E8.8.15.2", {"start": v(17, -36) * mm, "end": v(17, -33) * mm});
            skLineSegment(sketch, "E8.8.15.3", {"start": v(17, -33) * mm, "end": v(14, -33) * mm});
            skLineSegment(sketch, "E8.8.15.4", {"start": v(17, -36) * mm, "end": v(14, -36) * mm});
            skPoint(sketch, "E8.8.15.5", {"position": v(14, -33) * mm});
            skPoint(sketch, "E8.8.15.6", {"position": v(15.5, -34.5) * mm});
            skPoint(sketch, "E8.8.15.7", {"position": v(15.5, -34.5) * mm});
            skPoint(sketch, "E8.9.0.0", {"position": v(20, 34.5) * mm});
            skLineSegment(sketch, "E8.9.0.1", {"start": v(18.5, 33) * mm, "end": v(18.5, 36) * mm});
            skLineSegment(sketch, "E8.9.0.2", {"start": v(21.5, 33) * mm, "end": v(21.5, 36) * mm});
            skLineSegment(sketch, "E8.9.0.3", {"start": v(21.5, 36) * mm, "end": v(18.5, 36) * mm});
            skLineSegment(sketch, "E8.9.0.4", {"start": v(21.5, 33) * mm, "end": v(18.5, 33) * mm});
            skPoint(sketch, "E8.9.0.5", {"position": v(18.5, 36) * mm});
            skPoint(sketch, "E8.9.0.6", {"position": v(20, 34.5) * mm});
            skPoint(sketch, "E8.9.0.7", {"position": v(20, 34.5) * mm});
            skPoint(sketch, "E8.9.1.0", {"position": v(20, 29.9) * mm});
            skLineSegment(sketch, "E8.9.1.1", {"start": v(18.5, 28.4) * mm, "end": v(18.5, 31.4) * mm});
            skLineSegment(sketch, "E8.9.1.2", {"start": v(21.5, 28.4) * mm, "end": v(21.5, 31.4) * mm});
            skLineSegment(sketch, "E8.9.1.3", {"start": v(21.5, 31.4) * mm, "end": v(18.5, 31.4) * mm});
            skLineSegment(sketch, "E8.9.1.4", {"start": v(21.5, 28.4) * mm, "end": v(18.5, 28.4) * mm});
            skPoint(sketch, "E8.9.1.5", {"position": v(18.5, 31.4) * mm});
            skPoint(sketch, "E8.9.1.6", {"position": v(20, 29.9) * mm});
            skPoint(sketch, "E8.9.1.7", {"position": v(20, 29.9) * mm});
            skPoint(sketch, "E8.9.2.0", {"position": v(20, 25.3) * mm});
            skLineSegment(sketch, "E8.9.2.1", {"start": v(18.5, 23.8) * mm, "end": v(18.5, 26.8) * mm});
            skLineSegment(sketch, "E8.9.2.2", {"start": v(21.5, 23.8) * mm, "end": v(21.5, 26.8) * mm});
            skLineSegment(sketch, "E8.9.2.3", {"start": v(21.5, 26.8) * mm, "end": v(18.5, 26.8) * mm});
            skLineSegment(sketch, "E8.9.2.4", {"start": v(21.5, 23.8) * mm, "end": v(18.5, 23.8) * mm});
            skPoint(sketch, "E8.9.2.5", {"position": v(18.5, 26.8) * mm});
            skPoint(sketch, "E8.9.2.6", {"position": v(20, 25.3) * mm});
            skPoint(sketch, "E8.9.2.7", {"position": v(20, 25.3) * mm});
            skPoint(sketch, "E8.9.3.0", {"position": v(20, 20.7) * mm});
            skLineSegment(sketch, "E8.9.3.1", {"start": v(18.5, 19.2) * mm, "end": v(18.5, 22.2) * mm});
            skLineSegment(sketch, "E8.9.3.2", {"start": v(21.5, 19.2) * mm, "end": v(21.5, 22.2) * mm});
            skLineSegment(sketch, "E8.9.3.3", {"start": v(21.5, 22.2) * mm, "end": v(18.5, 22.2) * mm});
            skLineSegment(sketch, "E8.9.3.4", {"start": v(21.5, 19.2) * mm, "end": v(18.5, 19.2) * mm});
            skPoint(sketch, "E8.9.3.5", {"position": v(18.5, 22.2) * mm});
            skPoint(sketch, "E8.9.3.6", {"position": v(20, 20.7) * mm});
            skPoint(sketch, "E8.9.3.7", {"position": v(20, 20.7) * mm});
            skPoint(sketch, "E8.9.4.0", {"position": v(20, 16.1) * mm});
            skLineSegment(sketch, "E8.9.4.1", {"start": v(18.5, 14.6) * mm, "end": v(18.5, 17.6) * mm});
            skLineSegment(sketch, "E8.9.4.2", {"start": v(21.5, 14.6) * mm, "end": v(21.5, 17.6) * mm});
            skLineSegment(sketch, "E8.9.4.3", {"start": v(21.5, 17.6) * mm, "end": v(18.5, 17.6) * mm});
            skLineSegment(sketch, "E8.9.4.4", {"start": v(21.5, 14.6) * mm, "end": v(18.5, 14.6) * mm});
            skPoint(sketch, "E8.9.4.5", {"position": v(18.5, 17.6) * mm});
            skPoint(sketch, "E8.9.4.6", {"position": v(20, 16.1) * mm});
            skPoint(sketch, "E8.9.4.7", {"position": v(20, 16.1) * mm});
            skPoint(sketch, "E8.9.5.0", {"position": v(20, 11.5) * mm});
            skLineSegment(sketch, "E8.9.5.1", {"start": v(18.5, 10) * mm, "end": v(18.5, 13) * mm});
            skLineSegment(sketch, "E8.9.5.2", {"start": v(21.5, 10) * mm, "end": v(21.5, 13) * mm});
            skLineSegment(sketch, "E8.9.5.3", {"start": v(21.5, 13) * mm, "end": v(18.5, 13) * mm});
            skLineSegment(sketch, "E8.9.5.4", {"start": v(21.5, 10) * mm, "end": v(18.5, 10) * mm});
            skPoint(sketch, "E8.9.5.5", {"position": v(18.5, 13) * mm});
            skPoint(sketch, "E8.9.5.6", {"position": v(20, 11.5) * mm});
            skPoint(sketch, "E8.9.5.7", {"position": v(20, 11.5) * mm});
            skPoint(sketch, "E8.9.6.0", {"position": v(20, 6.9) * mm});
            skLineSegment(sketch, "E8.9.6.1", {"start": v(18.5, 5.4) * mm, "end": v(18.5, 8.4) * mm});
            skLineSegment(sketch, "E8.9.6.2", {"start": v(21.5, 5.4) * mm, "end": v(21.5, 8.4) * mm});
            skLineSegment(sketch, "E8.9.6.3", {"start": v(21.5, 8.4) * mm, "end": v(18.5, 8.4) * mm});
            skLineSegment(sketch, "E8.9.6.4", {"start": v(21.5, 5.4) * mm, "end": v(18.5, 5.4) * mm});
            skPoint(sketch, "E8.9.6.5", {"position": v(18.5, 8.4) * mm});
            skPoint(sketch, "E8.9.6.6", {"position": v(20, 6.9) * mm});
            skPoint(sketch, "E8.9.6.7", {"position": v(20, 6.9) * mm});
            skPoint(sketch, "E8.9.7.0", {"position": v(20, 2.3) * mm});
            skLineSegment(sketch, "E8.9.7.1", {"start": v(18.5, 0.8) * mm, "end": v(18.5, 3.8) * mm});
            skLineSegment(sketch, "E8.9.7.2", {"start": v(21.5, 0.8) * mm, "end": v(21.5, 3.8) * mm});
            skLineSegment(sketch, "E8.9.7.3", {"start": v(21.5, 3.8) * mm, "end": v(18.5, 3.8) * mm});
            skLineSegment(sketch, "E8.9.7.4", {"start": v(21.5, 0.8) * mm, "end": v(18.5, 0.8) * mm});
            skPoint(sketch, "E8.9.7.5", {"position": v(18.5, 3.8) * mm});
            skPoint(sketch, "E8.9.7.6", {"position": v(20, 2.3) * mm});
            skPoint(sketch, "E8.9.7.7", {"position": v(20, 2.3) * mm});
            skPoint(sketch, "E8.9.8.0", {"position": v(20, -2.3) * mm});
            skLineSegment(sketch, "E8.9.8.1", {"start": v(18.5, -3.8) * mm, "end": v(18.5, -0.8) * mm});
            skLineSegment(sketch, "E8.9.8.2", {"start": v(21.5, -3.8) * mm, "end": v(21.5, -0.8) * mm});
            skLineSegment(sketch, "E8.9.8.3", {"start": v(21.5, -0.8) * mm, "end": v(18.5, -0.8) * mm});
            skLineSegment(sketch, "E8.9.8.4", {"start": v(21.5, -3.8) * mm, "end": v(18.5, -3.8) * mm});
            skPoint(sketch, "E8.9.8.5", {"position": v(18.5, -0.8) * mm});
            skPoint(sketch, "E8.9.8.6", {"position": v(20, -2.3) * mm});
            skPoint(sketch, "E8.9.8.7", {"position": v(20, -2.3) * mm});
            skPoint(sketch, "E8.9.9.0", {"position": v(20, -6.9) * mm});
            skLineSegment(sketch, "E8.9.9.1", {"start": v(18.5, -8.4) * mm, "end": v(18.5, -5.4) * mm});
            skLineSegment(sketch, "E8.9.9.2", {"start": v(21.5, -8.4) * mm, "end": v(21.5, -5.4) * mm});
            skLineSegment(sketch, "E8.9.9.3", {"start": v(21.5, -5.4) * mm, "end": v(18.5, -5.4) * mm});
            skLineSegment(sketch, "E8.9.9.4", {"start": v(21.5, -8.4) * mm, "end": v(18.5, -8.4) * mm});
            skPoint(sketch, "E8.9.9.5", {"position": v(18.5, -5.4) * mm});
            skPoint(sketch, "E8.9.9.6", {"position": v(20, -6.9) * mm});
            skPoint(sketch, "E8.9.9.7", {"position": v(20, -6.9) * mm});
            skPoint(sketch, "E8.9.10.0", {"position": v(20, -11.5) * mm});
            skLineSegment(sketch, "E8.9.10.1", {"start": v(18.5, -13) * mm, "end": v(18.5, -10) * mm});
            skLineSegment(sketch, "E8.9.10.2", {"start": v(21.5, -13) * mm, "end": v(21.5, -10) * mm});
            skLineSegment(sketch, "E8.9.10.3", {"start": v(21.5, -10) * mm, "end": v(18.5, -10) * mm});
            skLineSegment(sketch, "E8.9.10.4", {"start": v(21.5, -13) * mm, "end": v(18.5, -13) * mm});
            skPoint(sketch, "E8.9.10.5", {"position": v(18.5, -10) * mm});
            skPoint(sketch, "E8.9.10.6", {"position": v(20, -11.5) * mm});
            skPoint(sketch, "E8.9.10.7", {"position": v(20, -11.5) * mm});
            skPoint(sketch, "E8.9.11.0", {"position": v(20, -16.1) * mm});
            skLineSegment(sketch, "E8.9.11.1", {"start": v(18.5, -17.6) * mm, "end": v(18.5, -14.6) * mm});
            skLineSegment(sketch, "E8.9.11.2", {"start": v(21.5, -17.6) * mm, "end": v(21.5, -14.6) * mm});
            skLineSegment(sketch, "E8.9.11.3", {"start": v(21.5, -14.6) * mm, "end": v(18.5, -14.6) * mm});
            skLineSegment(sketch, "E8.9.11.4", {"start": v(21.5, -17.6) * mm, "end": v(18.5, -17.6) * mm});
            skPoint(sketch, "E8.9.11.5", {"position": v(18.5, -14.6) * mm});
            skPoint(sketch, "E8.9.11.6", {"position": v(20, -16.1) * mm});
            skPoint(sketch, "E8.9.11.7", {"position": v(20, -16.1) * mm});
            skPoint(sketch, "E8.9.12.0", {"position": v(20, -20.7) * mm});
            skLineSegment(sketch, "E8.9.12.1", {"start": v(18.5, -22.2) * mm, "end": v(18.5, -19.2) * mm});
            skLineSegment(sketch, "E8.9.12.2", {"start": v(21.5, -22.2) * mm, "end": v(21.5, -19.2) * mm});
            skLineSegment(sketch, "E8.9.12.3", {"start": v(21.5, -19.2) * mm, "end": v(18.5, -19.2) * mm});
            skLineSegment(sketch, "E8.9.12.4", {"start": v(21.5, -22.2) * mm, "end": v(18.5, -22.2) * mm});
            skPoint(sketch, "E8.9.12.5", {"position": v(18.5, -19.2) * mm});
            skPoint(sketch, "E8.9.12.6", {"position": v(20, -20.7) * mm});
            skPoint(sketch, "E8.9.12.7", {"position": v(20, -20.7) * mm});
            skPoint(sketch, "E8.9.13.0", {"position": v(20, -25.3) * mm});
            skLineSegment(sketch, "E8.9.13.1", {"start": v(18.5, -26.8) * mm, "end": v(18.5, -23.8) * mm});
            skLineSegment(sketch, "E8.9.13.2", {"start": v(21.5, -26.8) * mm, "end": v(21.5, -23.8) * mm});
            skLineSegment(sketch, "E8.9.13.3", {"start": v(21.5, -23.8) * mm, "end": v(18.5, -23.8) * mm});
            skLineSegment(sketch, "E8.9.13.4", {"start": v(21.5, -26.8) * mm, "end": v(18.5, -26.8) * mm});
            skPoint(sketch, "E8.9.13.5", {"position": v(18.5, -23.8) * mm});
            skPoint(sketch, "E8.9.13.6", {"position": v(20, -25.3) * mm});
            skPoint(sketch, "E8.9.13.7", {"position": v(20, -25.3) * mm});
            skPoint(sketch, "E8.9.14.0", {"position": v(20, -29.9) * mm});
            skLineSegment(sketch, "E8.9.14.1", {"start": v(18.5, -31.4) * mm, "end": v(18.5, -28.4) * mm});
            skLineSegment(sketch, "E8.9.14.2", {"start": v(21.5, -31.4) * mm, "end": v(21.5, -28.4) * mm});
            skLineSegment(sketch, "E8.9.14.3", {"start": v(21.5, -28.4) * mm, "end": v(18.5, -28.4) * mm});
            skLineSegment(sketch, "E8.9.14.4", {"start": v(21.5, -31.4) * mm, "end": v(18.5, -31.4) * mm});
            skPoint(sketch, "E8.9.14.5", {"position": v(18.5, -28.4) * mm});
            skPoint(sketch, "E8.9.14.6", {"position": v(20, -29.9) * mm});
            skPoint(sketch, "E8.9.14.7", {"position": v(20, -29.9) * mm});
            skPoint(sketch, "E8.9.15.0", {"position": v(20, -34.5) * mm});
            skLineSegment(sketch, "E8.9.15.1", {"start": v(18.5, -36) * mm, "end": v(18.5, -33) * mm});
            skLineSegment(sketch, "E8.9.15.2", {"start": v(21.5, -36) * mm, "end": v(21.5, -33) * mm});
            skLineSegment(sketch, "E8.9.15.3", {"start": v(21.5, -33) * mm, "end": v(18.5, -33) * mm});
            skLineSegment(sketch, "E8.9.15.4", {"start": v(21.5, -36) * mm, "end": v(18.5, -36) * mm});
            skPoint(sketch, "E8.9.15.5", {"position": v(18.5, -33) * mm});
            skPoint(sketch, "E8.9.15.6", {"position": v(20, -34.5) * mm});
            skPoint(sketch, "E8.9.15.7", {"position": v(20, -34.5) * mm});
            skLineSegment(sketch, "E8.direction1", {"start": v(-22, 33) * mm, "end": v(-17.5, 33) * mm, "construction": true});
            skLineSegment(sketch, "E8.direction2", {"start": v(-22, 33) * mm, "end": v(-22, 28.4) * mm, "construction": true});
            skSolve(sketch);
        }
        {
            var Q0;
            Q0=makeQuery(id+"F0.imprint","IMPRINT",FACE,{"disambiguationData":[TD([[makeQuery(id+"F0.imprint","IMPRINT",EDGE,{"derivedFrom":sQuery(id+"F0.wireOp",EDGE,"E0.bottom")}),-1.0]])]});
            extrude(context, id + "F1", {"entities" : qUnion([Q0]), "depth" : 2 * mm});
        }
    });
